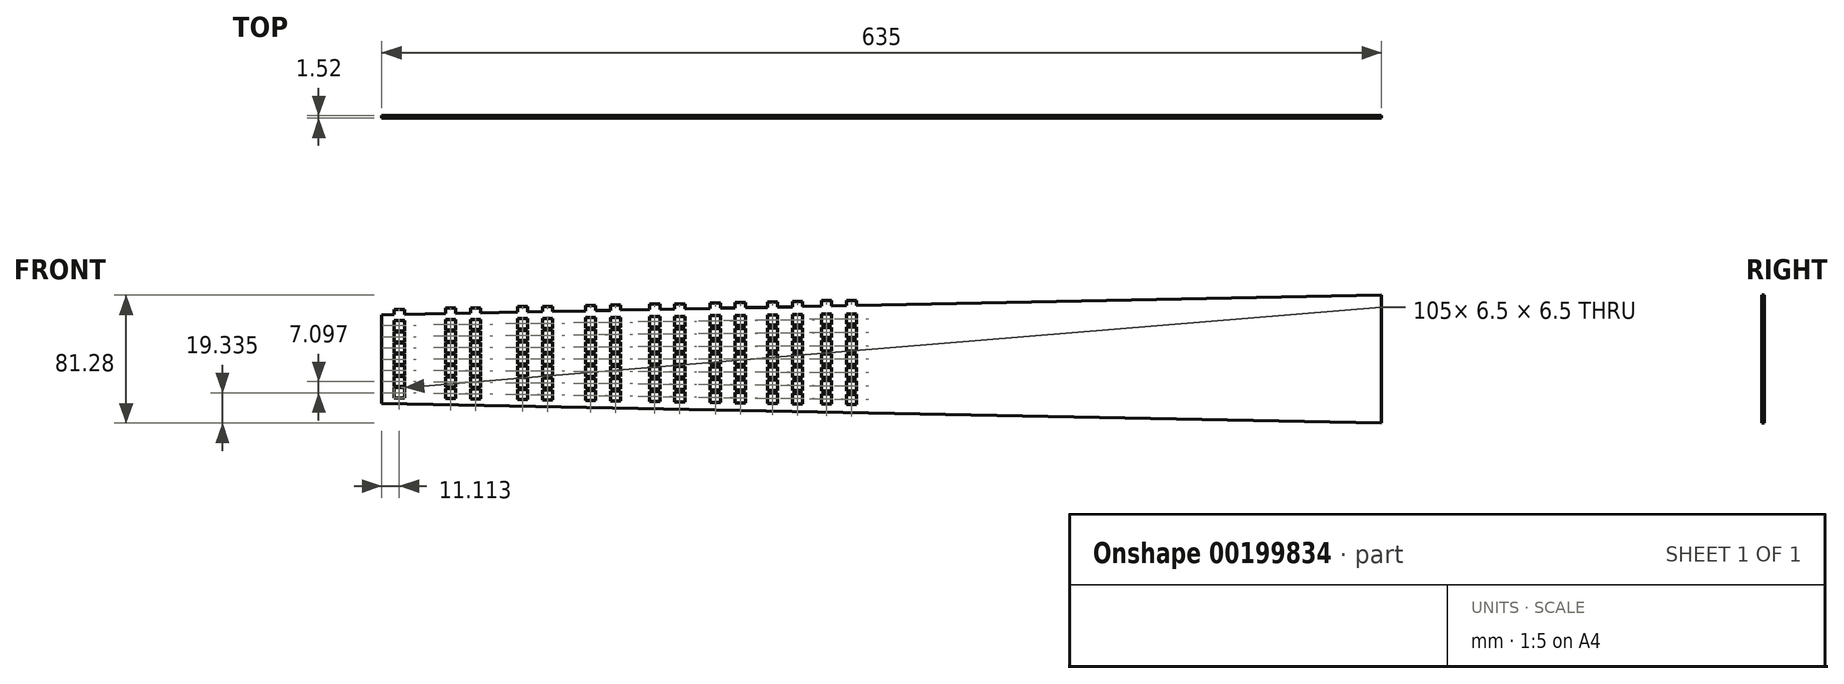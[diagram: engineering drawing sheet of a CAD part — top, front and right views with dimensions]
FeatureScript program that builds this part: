
annotation { "Feature Type Name" : "Feature", "Feature Type Description" : "" }
export const myFeature = defineFeature(function(context is Context, id is Id, definition is map)
    precondition{}
    {
        {
            var Q0;
            Q0=qCreatedBy(makeId("Front.planeOp"),FACE);
            var sketch = newSketch(context, id + "F0", { "sketchPlane" : qUnion([Q0])});
            skLineSegment(sketch, "E0", {"start": v(0, 0) * mm, "end": v(0, 56.39) * mm});
            skLineSegment(sketch, "E1", {"start": v(0, 56.39) * mm, "end": v(304.8, 62.36) * mm});
            skLineSegment(sketch, "E2", {"start": v(635, 68.83) * mm, "end": v(635, -12.45) * mm});
            skLineSegment(sketch, "E3", {"start": v(635, -12.45) * mm, "end": v(304.8, -5.97) * mm});
            skLineSegment(sketch, "E4", {"start": v(0, 28.2) * mm, "end": v(897.35, 28.2) * mm, "construction": true});
            skLineSegment(sketch, "E5", {"start": v(0, 7.05) * mm, "end": v(635, -2.29) * mm, "construction": true});
            skLineSegment(sketch, "E6", {"start": v(0, 21.15) * mm, "end": v(635, 18.03) * mm, "construction": true});
            skLineSegment(sketch, "E7", {"start": v(0, 35.24) * mm, "end": v(635, 38.35) * mm, "construction": true});
            skLineSegment(sketch, "E8", {"start": v(0, 49.34) * mm, "end": v(635, 58.67) * mm, "construction": true});
            skLineSegment(sketch, "E9", {"start": v(11.11, -8.07) * mm, "end": v(11.11, 65.52) * mm, "construction": true});
            skLineSegment(sketch, "E10", {"start": v(59.58, -8.48) * mm, "end": v(59.58, 66.34) * mm, "construction": true});
            skLineSegment(sketch, "E11", {"start": v(43.7, -5.78) * mm, "end": v(43.7, 64.91) * mm, "construction": true});
            skPoint(sketch, "E12", {"position": v(11.11, 6.89) * mm});
            skLineSegment(sketch, "E13.bottom", {"start": v(7.86, 10.14) * mm, "end": v(14.36, 10.14) * mm});
            skLineSegment(sketch, "E13.top", {"start": v(7.86, 3.64) * mm, "end": v(14.36, 3.64) * mm});
            skLineSegment(sketch, "E13.left", {"start": v(7.86, 10.14) * mm, "end": v(7.86, 3.64) * mm});
            skLineSegment(sketch, "E13.right", {"start": v(14.36, 10.14) * mm, "end": v(14.36, 3.64) * mm});
            skLineSegment(sketch, "E14.direction2", {"start": v(7.86, 10.14) * mm, "end": v(7.86, 17.25) * mm, "construction": true});
            skLineSegment(sketch, "E15.bottom", {"start": v(40.46, 9.66) * mm, "end": v(46.96, 9.66) * mm});
            skLineSegment(sketch, "E15.top", {"start": v(40.46, 3.16) * mm, "end": v(46.96, 3.16) * mm});
            skLineSegment(sketch, "E15.left", {"start": v(40.46, 9.66) * mm, "end": v(40.46, 3.16) * mm});
            skLineSegment(sketch, "E15.right", {"start": v(46.96, 9.66) * mm, "end": v(46.96, 3.16) * mm});
            skPoint(sketch, "E15.middle", {"position": v(43.7, 6.4) * mm});
            skLineSegment(sketch, "E16.bottom", {"start": v(62.83, 9.42) * mm, "end": v(56.33, 9.42) * mm});
            skLineSegment(sketch, "E16.top", {"start": v(62.83, 2.92) * mm, "end": v(56.33, 2.92) * mm});
            skLineSegment(sketch, "E16.left", {"start": v(62.83, 9.42) * mm, "end": v(62.83, 2.92) * mm});
            skLineSegment(sketch, "E16.right", {"start": v(56.33, 9.42) * mm, "end": v(56.33, 2.92) * mm});
            skPoint(sketch, "E16.middle", {"position": v(59.58, 6.17) * mm});
            skPoint(sketch, "E17", {"position": v(43.7, 20.93) * mm});
            skPoint(sketch, "E18", {"position": v(59.58, 20.85) * mm});
            skLineSegment(sketch, "E19", {"start": v(89.46, -9.6) * mm, "end": v(89.46, 71.58) * mm, "construction": true});
            skLineSegment(sketch, "E20", {"start": v(105.33, -10.34) * mm, "end": v(105.33, 69.93) * mm, "construction": true});
            skLineSegment(sketch, "E21", {"start": v(132.64, -17.59) * mm, "end": v(132.64, 74.26) * mm, "construction": true});
            skLineSegment(sketch, "E22", {"start": v(148.51, -17.59) * mm, "end": v(148.51, 69.02) * mm, "construction": true});
            skLineSegment(sketch, "E23", {"start": v(173.4, -18.82) * mm, "end": v(173.4, 73.33) * mm, "construction": true});
            skLineSegment(sketch, "E24", {"start": v(189.27, -16.66) * mm, "end": v(189.27, 66.86) * mm, "construction": true});
            skLineSegment(sketch, "E25", {"start": v(451.27, -15.83) * mm, "end": v(451.27, 70.28) * mm, "construction": true});
            skLineSegment(sketch, "E26", {"start": v(227.74, -18.15) * mm, "end": v(227.74, 69.99) * mm, "construction": true});
            skLineSegment(sketch, "E27", {"start": v(264.05, -13.9) * mm, "end": v(264.05, 74.15) * mm, "construction": true});
            skLineSegment(sketch, "E28", {"start": v(298.33, -16.5) * mm, "end": v(298.33, 71.54) * mm, "construction": true});
            skLineSegment(sketch, "E29", {"start": v(330.68, -19.56) * mm, "end": v(330.68, 75.46) * mm, "construction": true});
            skLineSegment(sketch, "E30", {"start": v(361.21, -17.9) * mm, "end": v(361.21, 72.97) * mm, "construction": true});
            skLineSegment(sketch, "E31", {"start": v(390.03, -19.02) * mm, "end": v(390.03, 73.96) * mm, "construction": true});
            skLineSegment(sketch, "E32", {"start": v(417.24, -23.13) * mm, "end": v(417.24, 74.37) * mm, "construction": true});
            skLineSegment(sketch, "E33", {"start": v(442.91, -24.9) * mm, "end": v(442.91, 73.26) * mm, "construction": true});
            skLineSegment(sketch, "E34", {"start": v(467.15, -27.86) * mm, "end": v(467.15, 72.83) * mm, "construction": true});
            skLineSegment(sketch, "E35", {"start": v(492.88, -29.16) * mm, "end": v(492.88, 78.06) * mm, "construction": true});
            skLineSegment(sketch, "E36", {"start": v(513.87, -22.04) * mm, "end": v(513.87, 76.59) * mm, "construction": true});
            skLineSegment(sketch, "E37", {"start": v(533.67, -25.93) * mm, "end": v(533.67, 79.32) * mm, "construction": true});
            skLineSegment(sketch, "E38", {"start": v(602.4, -21.27) * mm, "end": v(602.4, 83.2) * mm, "construction": true});
            skLineSegment(sketch, "E39", {"start": v(570.01, -19.88) * mm, "end": v(570.01, 78.37) * mm, "construction": true});
            skLineSegment(sketch, "E40", {"start": v(586.67, -17.8) * mm, "end": v(586.67, 83.9) * mm, "construction": true});
            skLineSegment(sketch, "E41", {"start": v(552.37, -18.5) * mm, "end": v(552.37, 94.16) * mm, "construction": true});
            skPoint(sketch, "E42", {"position": v(89.46, 5.73) * mm});
            skPoint(sketch, "E43", {"position": v(89.46, 20.7) * mm});
            skPoint(sketch, "E44", {"position": v(105.33, 20.63) * mm});
            skPoint(sketch, "E45", {"position": v(105.33, 5.5) * mm});
            skPoint(sketch, "E46", {"position": v(132.64, 20.5) * mm});
            skPoint(sketch, "E47", {"position": v(132.64, 5.1) * mm});
            skPoint(sketch, "E48", {"position": v(148.51, 20.42) * mm});
            skPoint(sketch, "E49", {"position": v(148.51, 4.87) * mm});
            skPoint(sketch, "E50", {"position": v(173.4, 20.3) * mm});
            skPoint(sketch, "E51", {"position": v(173.4, 4.5) * mm});
            skPoint(sketch, "E52", {"position": v(189.27, 20.22) * mm});
            skPoint(sketch, "E53", {"position": v(227.74, 20.03) * mm});
            skPoint(sketch, "E54", {"position": v(227.74, 3.7) * mm});
            skLineSegment(sketch, "E55", {"start": v(304.8, -5.97) * mm, "end": v(304.8, 62.36) * mm});
            skLineSegment(sketch, "E56", {"start": v(211.87, -18.15) * mm, "end": v(211.87, 88.54) * mm, "construction": true});
            skLineSegment(sketch, "E57", {"start": v(248.18, -17.72) * mm, "end": v(248.18, 84.91) * mm, "construction": true});
            skLineSegment(sketch, "E58", {"start": v(282.45, -20.3) * mm, "end": v(282.45, 79.21) * mm, "construction": true});
            skPoint(sketch, "E59", {"position": v(298.33, 2.66) * mm});
            skPoint(sketch, "E60", {"position": v(298.33, 19.68) * mm});
            skPoint(sketch, "E61", {"position": v(282.45, 19.76) * mm});
            skPoint(sketch, "E62", {"position": v(282.45, 2.9) * mm});
            skPoint(sketch, "E63", {"position": v(264.05, 3.17) * mm});
            skPoint(sketch, "E64", {"position": v(264.05, 19.85) * mm});
            skPoint(sketch, "E65", {"position": v(248.18, 19.93) * mm});
            skPoint(sketch, "E66", {"position": v(248.18, 3.4) * mm});
            skPoint(sketch, "E67", {"position": v(211.87, 20.1) * mm});
            skPoint(sketch, "E68", {"position": v(211.87, 3.93) * mm});
            skLineSegment(sketch, "E69.bottom", {"start": v(86.2, 8.98) * mm, "end": v(92.7, 8.98) * mm});
            skLineSegment(sketch, "E69.top", {"start": v(86.2, 2.48) * mm, "end": v(92.7, 2.48) * mm});
            skLineSegment(sketch, "E69.left", {"start": v(86.2, 8.98) * mm, "end": v(86.2, 2.48) * mm});
            skLineSegment(sketch, "E69.right", {"start": v(92.7, 8.98) * mm, "end": v(92.7, 2.48) * mm});
            skLineSegment(sketch, "E70.bottom", {"start": v(102.08, 8.75) * mm, "end": v(108.58, 8.75) * mm});
            skLineSegment(sketch, "E70.top", {"start": v(102.08, 2.25) * mm, "end": v(108.58, 2.25) * mm});
            skLineSegment(sketch, "E70.left", {"start": v(102.08, 8.75) * mm, "end": v(102.08, 2.25) * mm});
            skLineSegment(sketch, "E70.right", {"start": v(108.58, 8.75) * mm, "end": v(108.58, 2.25) * mm});
            skLineSegment(sketch, "E71.bottom", {"start": v(129.39, 8.35) * mm, "end": v(135.89, 8.35) * mm});
            skLineSegment(sketch, "E71.top", {"start": v(129.39, 1.85) * mm, "end": v(135.89, 1.85) * mm});
            skLineSegment(sketch, "E71.left", {"start": v(129.39, 8.35) * mm, "end": v(129.39, 1.85) * mm});
            skLineSegment(sketch, "E71.right", {"start": v(135.89, 8.35) * mm, "end": v(135.89, 1.85) * mm});
            skLineSegment(sketch, "E72.bottom", {"start": v(145.26, 8.12) * mm, "end": v(151.76, 8.12) * mm});
            skLineSegment(sketch, "E72.top", {"start": v(145.26, 1.62) * mm, "end": v(151.76, 1.62) * mm});
            skLineSegment(sketch, "E72.left", {"start": v(145.26, 8.12) * mm, "end": v(145.26, 1.62) * mm});
            skLineSegment(sketch, "E72.right", {"start": v(151.76, 8.12) * mm, "end": v(151.76, 1.62) * mm});
            skLineSegment(sketch, "E73.bottom", {"start": v(208.62, 7.18) * mm, "end": v(215.12, 7.18) * mm});
            skLineSegment(sketch, "E73.top", {"start": v(208.62, 0.68) * mm, "end": v(215.12, 0.68) * mm});
            skLineSegment(sketch, "E73.left", {"start": v(208.62, 7.18) * mm, "end": v(208.62, 0.68) * mm});
            skLineSegment(sketch, "E73.right", {"start": v(215.12, 7.18) * mm, "end": v(215.12, 0.68) * mm});
            skLineSegment(sketch, "E74.bottom", {"start": v(224.5, 6.95) * mm, "end": v(231, 6.95) * mm});
            skLineSegment(sketch, "E74.top", {"start": v(224.5, 0.45) * mm, "end": v(231, 0.45) * mm});
            skLineSegment(sketch, "E74.left", {"start": v(224.5, 6.95) * mm, "end": v(224.5, 0.45) * mm});
            skLineSegment(sketch, "E74.right", {"start": v(231, 6.95) * mm, "end": v(231, 0.45) * mm});
            skLineSegment(sketch, "E75.bottom", {"start": v(244.93, 6.65) * mm, "end": v(251.43, 6.65) * mm});
            skLineSegment(sketch, "E75.top", {"start": v(244.93, 0.15) * mm, "end": v(251.43, 0.15) * mm});
            skLineSegment(sketch, "E75.left", {"start": v(244.93, 6.65) * mm, "end": v(244.93, 0.15) * mm});
            skLineSegment(sketch, "E75.right", {"start": v(251.43, 6.65) * mm, "end": v(251.43, 0.15) * mm});
            skLineSegment(sketch, "E76.bottom", {"start": v(260.8, 6.42) * mm, "end": v(267.3, 6.42) * mm});
            skLineSegment(sketch, "E76.top", {"start": v(260.8, -0.08) * mm, "end": v(267.3, -0.08) * mm});
            skLineSegment(sketch, "E76.left", {"start": v(260.8, 6.42) * mm, "end": v(260.8, -0.08) * mm});
            skLineSegment(sketch, "E76.right", {"start": v(267.3, 6.42) * mm, "end": v(267.3, -0.08) * mm});
            skLineSegment(sketch, "E77.bottom", {"start": v(279.2, 6.15) * mm, "end": v(285.7, 6.15) * mm});
            skLineSegment(sketch, "E77.top", {"start": v(279.2, -0.35) * mm, "end": v(285.7, -0.35) * mm});
            skLineSegment(sketch, "E77.left", {"start": v(279.2, 6.15) * mm, "end": v(279.2, -0.35) * mm});
            skLineSegment(sketch, "E77.right", {"start": v(285.7, 6.15) * mm, "end": v(285.7, -0.35) * mm});
            skLineSegment(sketch, "E78.bottom", {"start": v(295.08, 5.91) * mm, "end": v(301.58, 5.91) * mm});
            skLineSegment(sketch, "E78.top", {"start": v(295.08, -0.59) * mm, "end": v(301.58, -0.59) * mm});
            skLineSegment(sketch, "E78.left", {"start": v(295.08, 5.91) * mm, "end": v(295.08, -0.59) * mm});
            skLineSegment(sketch, "E78.right", {"start": v(301.58, 5.91) * mm, "end": v(301.58, -0.59) * mm});
            skLineSegment(sketch, "E79.bottom", {"start": v(170.14, 7.75) * mm, "end": v(176.64, 7.75) * mm});
            skLineSegment(sketch, "E79.top", {"start": v(170.14, 1.25) * mm, "end": v(176.64, 1.25) * mm});
            skLineSegment(sketch, "E79.left", {"start": v(170.14, 7.75) * mm, "end": v(170.14, 1.25) * mm});
            skLineSegment(sketch, "E79.right", {"start": v(176.64, 7.75) * mm, "end": v(176.64, 1.25) * mm});
            skPoint(sketch, "E80", {"position": v(304.8, 62.36) * mm});
            skPoint(sketch, "E81", {"position": v(304.8, -5.97) * mm});
            skPoint(sketch, "E82.orphan", {"position": v(304.8, 80.2) * mm});
            skLineSegment(sketch, "E83", {"start": v(304.8, 62.36) * mm, "end": v(635, 68.83) * mm});
            skLineSegment(sketch, "E84", {"start": v(304.8, -5.97) * mm, "end": v(0, 0) * mm});
            skLineSegment(sketch, "E85.0.1.0", {"start": v(40.46, 16.94) * mm, "end": v(46.96, 16.94) * mm});
            skLineSegment(sketch, "E85.0.1.1", {"start": v(40.46, 16.94) * mm, "end": v(40.46, 10.44) * mm});
            skLineSegment(sketch, "E85.0.1.2", {"start": v(46.96, 16.94) * mm, "end": v(46.96, 10.44) * mm});
            skLineSegment(sketch, "E85.0.1.3", {"start": v(40.46, 10.44) * mm, "end": v(46.96, 10.44) * mm});
            skLineSegment(sketch, "E85.0.2.0", {"start": v(40.46, 24.23) * mm, "end": v(46.96, 24.23) * mm});
            skLineSegment(sketch, "E85.0.2.1", {"start": v(40.46, 24.23) * mm, "end": v(40.46, 17.73) * mm});
            skLineSegment(sketch, "E85.0.2.2", {"start": v(46.96, 24.23) * mm, "end": v(46.96, 17.73) * mm});
            skLineSegment(sketch, "E85.0.2.3", {"start": v(40.46, 17.73) * mm, "end": v(46.96, 17.73) * mm});
            skLineSegment(sketch, "E85.0.3.0", {"start": v(40.46, 31.52) * mm, "end": v(46.96, 31.52) * mm});
            skLineSegment(sketch, "E85.0.3.1", {"start": v(40.46, 31.52) * mm, "end": v(40.46, 25.02) * mm});
            skLineSegment(sketch, "E85.0.3.2", {"start": v(46.96, 31.52) * mm, "end": v(46.96, 25.02) * mm});
            skLineSegment(sketch, "E85.0.3.3", {"start": v(40.46, 25.02) * mm, "end": v(46.96, 25.02) * mm});
            skLineSegment(sketch, "E85.direction1", {"start": v(40.46, 9.66) * mm, "end": v(65.86, 9.66) * mm, "construction": true});
            skLineSegment(sketch, "E85.direction2", {"start": v(40.46, 9.66) * mm, "end": v(40.46, 16.94) * mm, "construction": true});
            skLineSegment(sketch, "E86.0.1.0", {"start": v(56.33, 16.77) * mm, "end": v(56.33, 10.27) * mm});
            skLineSegment(sketch, "E86.0.1.1", {"start": v(62.83, 10.27) * mm, "end": v(56.33, 10.27) * mm});
            skLineSegment(sketch, "E86.0.1.2", {"start": v(62.83, 16.77) * mm, "end": v(56.33, 16.77) * mm});
            skLineSegment(sketch, "E86.0.1.3", {"start": v(62.83, 16.77) * mm, "end": v(62.83, 10.27) * mm});
            skPoint(sketch, "E86.0.1.4", {"position": v(59.58, 13.52) * mm});
            skLineSegment(sketch, "E86.0.2.0", {"start": v(56.33, 24.12) * mm, "end": v(56.33, 17.62) * mm});
            skLineSegment(sketch, "E86.0.2.1", {"start": v(62.83, 17.62) * mm, "end": v(56.33, 17.62) * mm});
            skLineSegment(sketch, "E86.0.2.2", {"start": v(62.83, 24.12) * mm, "end": v(56.33, 24.12) * mm});
            skLineSegment(sketch, "E86.0.2.3", {"start": v(62.83, 24.12) * mm, "end": v(62.83, 17.62) * mm});
            skPoint(sketch, "E86.0.2.4", {"position": v(59.58, 20.87) * mm});
            skLineSegment(sketch, "E86.0.3.0", {"start": v(56.33, 31.47) * mm, "end": v(56.33, 24.97) * mm});
            skLineSegment(sketch, "E86.0.3.1", {"start": v(62.83, 24.97) * mm, "end": v(56.33, 24.97) * mm});
            skLineSegment(sketch, "E86.0.3.2", {"start": v(62.83, 31.47) * mm, "end": v(56.33, 31.47) * mm});
            skLineSegment(sketch, "E86.0.3.3", {"start": v(62.83, 31.47) * mm, "end": v(62.83, 24.97) * mm});
            skPoint(sketch, "E86.0.3.4", {"position": v(59.58, 28.22) * mm});
            skLineSegment(sketch, "E86.direction1", {"start": v(56.33, 2.92) * mm, "end": v(83.32, 2.92) * mm, "construction": true});
            skLineSegment(sketch, "E86.direction2", {"start": v(56.33, 2.92) * mm, "end": v(56.33, 10.27) * mm, "construction": true});
            skLineSegment(sketch, "E87.0.1.0", {"start": v(86.2, 10) * mm, "end": v(92.7, 10) * mm});
            skLineSegment(sketch, "E87.0.1.1", {"start": v(92.7, 16.5) * mm, "end": v(92.7, 10) * mm});
            skPoint(sketch, "E87.0.1.2", {"position": v(89.46, 13.24) * mm});
            skLineSegment(sketch, "E87.0.1.3", {"start": v(86.2, 16.5) * mm, "end": v(86.2, 10) * mm});
            skLineSegment(sketch, "E87.0.1.4", {"start": v(86.2, 16.5) * mm, "end": v(92.7, 16.5) * mm});
            skPoint(sketch, "E87.0.1.5", {"position": v(89.46, 13.24) * mm});
            skLineSegment(sketch, "E87.0.2.0", {"start": v(86.2, 17.5) * mm, "end": v(92.7, 17.5) * mm});
            skLineSegment(sketch, "E87.0.2.1", {"start": v(92.7, 24) * mm, "end": v(92.7, 17.5) * mm});
            skPoint(sketch, "E87.0.2.2", {"position": v(89.46, 20.76) * mm});
            skLineSegment(sketch, "E87.0.2.3", {"start": v(86.2, 24) * mm, "end": v(86.2, 17.5) * mm});
            skLineSegment(sketch, "E87.0.2.4", {"start": v(86.2, 24) * mm, "end": v(92.7, 24) * mm});
            skPoint(sketch, "E87.0.2.5", {"position": v(89.46, 20.76) * mm});
            skLineSegment(sketch, "E87.0.3.0", {"start": v(86.2, 25.02) * mm, "end": v(92.7, 25.02) * mm});
            skLineSegment(sketch, "E87.0.3.1", {"start": v(92.7, 31.52) * mm, "end": v(92.7, 25.02) * mm});
            skPoint(sketch, "E87.0.3.2", {"position": v(89.46, 28.27) * mm});
            skLineSegment(sketch, "E87.0.3.3", {"start": v(86.2, 31.52) * mm, "end": v(86.2, 25.02) * mm});
            skLineSegment(sketch, "E87.0.3.4", {"start": v(86.2, 31.52) * mm, "end": v(92.7, 31.52) * mm});
            skPoint(sketch, "E87.0.3.5", {"position": v(89.46, 28.27) * mm});
            skLineSegment(sketch, "E87.direction1", {"start": v(86.2, 2.48) * mm, "end": v(111.6, 2.48) * mm, "construction": true});
            skLineSegment(sketch, "E87.direction2", {"start": v(86.2, 2.48) * mm, "end": v(86.2, 10) * mm, "construction": true});
            skLineSegment(sketch, "E88.0.1.0", {"start": v(102.08, 9.82) * mm, "end": v(108.58, 9.82) * mm});
            skLineSegment(sketch, "E88.0.1.1", {"start": v(102.08, 16.32) * mm, "end": v(102.08, 9.82) * mm});
            skLineSegment(sketch, "E88.0.1.2", {"start": v(102.08, 16.32) * mm, "end": v(108.58, 16.32) * mm});
            skLineSegment(sketch, "E88.0.1.3", {"start": v(108.58, 16.32) * mm, "end": v(108.58, 9.82) * mm});
            skPoint(sketch, "E88.0.1.4", {"position": v(105.33, 13.07) * mm});
            skPoint(sketch, "E88.0.1.5", {"position": v(105.33, 13.07) * mm});
            skLineSegment(sketch, "E88.0.2.0", {"start": v(102.08, 17.4) * mm, "end": v(108.58, 17.4) * mm});
            skLineSegment(sketch, "E88.0.2.1", {"start": v(102.08, 23.9) * mm, "end": v(102.08, 17.4) * mm});
            skLineSegment(sketch, "E88.0.2.2", {"start": v(102.08, 23.9) * mm, "end": v(108.58, 23.9) * mm});
            skLineSegment(sketch, "E88.0.2.3", {"start": v(108.58, 23.9) * mm, "end": v(108.58, 17.4) * mm});
            skPoint(sketch, "E88.0.2.4", {"position": v(105.33, 20.64) * mm});
            skPoint(sketch, "E88.0.2.5", {"position": v(105.33, 20.64) * mm});
            skLineSegment(sketch, "E88.0.3.0", {"start": v(102.08, 24.97) * mm, "end": v(108.58, 24.97) * mm});
            skLineSegment(sketch, "E88.0.3.1", {"start": v(102.08, 31.47) * mm, "end": v(102.08, 24.97) * mm});
            skLineSegment(sketch, "E88.0.3.2", {"start": v(102.08, 31.47) * mm, "end": v(108.58, 31.47) * mm});
            skLineSegment(sketch, "E88.0.3.3", {"start": v(108.58, 31.47) * mm, "end": v(108.58, 24.97) * mm});
            skPoint(sketch, "E88.0.3.4", {"position": v(105.33, 28.22) * mm});
            skPoint(sketch, "E88.0.3.5", {"position": v(105.33, 28.22) * mm});
            skLineSegment(sketch, "E88.direction1", {"start": v(102.08, 2.25) * mm, "end": v(127.48, 2.25) * mm, "construction": true});
            skLineSegment(sketch, "E88.direction2", {"start": v(102.08, 2.25) * mm, "end": v(102.08, 9.82) * mm, "construction": true});
            skLineSegment(sketch, "E89.0.0.4", {"start": v(86.2, 32.53) * mm, "end": v(92.7, 32.53) * mm});
            skLineSegment(sketch, "E89.3.0.4", {"start": v(92.7, 39.03) * mm, "end": v(92.7, 32.53) * mm});
            skPoint(sketch, "E89.6.0.4", {"position": v(89.46, 35.78) * mm});
            skLineSegment(sketch, "E89.7.0.4", {"start": v(86.2, 39.03) * mm, "end": v(86.2, 32.53) * mm});
            skLineSegment(sketch, "E89.10.0.4", {"start": v(86.2, 39.03) * mm, "end": v(92.7, 39.03) * mm});
            skPoint(sketch, "E89.13.0.4", {"position": v(89.46, 35.78) * mm});
            skLineSegment(sketch, "E89.0.0.5", {"start": v(86.2, 40.04) * mm, "end": v(92.7, 40.04) * mm});
            skLineSegment(sketch, "E89.3.0.5", {"start": v(92.7, 46.54) * mm, "end": v(92.7, 40.04) * mm});
            skPoint(sketch, "E89.6.0.5", {"position": v(89.46, 43.29) * mm});
            skLineSegment(sketch, "E89.7.0.5", {"start": v(86.2, 46.54) * mm, "end": v(86.2, 40.04) * mm});
            skLineSegment(sketch, "E89.10.0.5", {"start": v(86.2, 46.54) * mm, "end": v(92.7, 46.54) * mm});
            skPoint(sketch, "E89.13.0.5", {"position": v(89.46, 43.29) * mm});
            skLineSegment(sketch, "E89.0.0.6", {"start": v(86.2, 47.55) * mm, "end": v(92.7, 47.55) * mm});
            skLineSegment(sketch, "E89.3.0.6", {"start": v(92.7, 54.05) * mm, "end": v(92.7, 47.55) * mm});
            skPoint(sketch, "E89.6.0.6", {"position": v(89.46, 50.8) * mm});
            skLineSegment(sketch, "E89.7.0.6", {"start": v(86.2, 54.05) * mm, "end": v(86.2, 47.55) * mm});
            skLineSegment(sketch, "E89.10.0.6", {"start": v(86.2, 54.05) * mm, "end": v(92.7, 54.05) * mm});
            skPoint(sketch, "E89.13.0.6", {"position": v(89.46, 50.8) * mm});
            skLineSegment(sketch, "E89.0.0.7", {"start": v(86.2, 55.06) * mm, "end": v(92.7, 55.06) * mm});
            skLineSegment(sketch, "E89.3.0.7", {"start": v(92.7, 61.56) * mm, "end": v(92.7, 55.06) * mm});
            skPoint(sketch, "E89.6.0.7", {"position": v(89.46, 58.3) * mm});
            skLineSegment(sketch, "E89.7.0.7", {"start": v(86.2, 61.56) * mm, "end": v(86.2, 55.06) * mm});
            skLineSegment(sketch, "E89.10.0.7", {"start": v(86.2, 61.56) * mm, "end": v(92.7, 61.56) * mm});
            skPoint(sketch, "E89.13.0.7", {"position": v(89.46, 58.3) * mm});
            skLineSegment(sketch, "E90.0.0.4", {"start": v(40.46, 38.8) * mm, "end": v(46.96, 38.8) * mm});
            skLineSegment(sketch, "E90.3.0.4", {"start": v(40.46, 38.8) * mm, "end": v(40.46, 32.3) * mm});
            skLineSegment(sketch, "E90.6.0.4", {"start": v(46.96, 38.8) * mm, "end": v(46.96, 32.3) * mm});
            skLineSegment(sketch, "E90.9.0.4", {"start": v(40.46, 32.3) * mm, "end": v(46.96, 32.3) * mm});
            skLineSegment(sketch, "E90.0.0.5", {"start": v(40.46, 46.1) * mm, "end": v(46.96, 46.1) * mm});
            skLineSegment(sketch, "E90.3.0.5", {"start": v(40.46, 46.1) * mm, "end": v(40.46, 39.6) * mm});
            skLineSegment(sketch, "E90.6.0.5", {"start": v(46.96, 46.1) * mm, "end": v(46.96, 39.6) * mm});
            skLineSegment(sketch, "E90.9.0.5", {"start": v(40.46, 39.6) * mm, "end": v(46.96, 39.6) * mm});
            skLineSegment(sketch, "E90.0.0.6", {"start": v(40.46, 53.38) * mm, "end": v(46.96, 53.38) * mm});
            skLineSegment(sketch, "E90.3.0.6", {"start": v(40.46, 53.38) * mm, "end": v(40.46, 46.88) * mm});
            skLineSegment(sketch, "E90.6.0.6", {"start": v(46.96, 53.38) * mm, "end": v(46.96, 46.88) * mm});
            skLineSegment(sketch, "E90.9.0.6", {"start": v(40.46, 46.88) * mm, "end": v(46.96, 46.88) * mm});
            skLineSegment(sketch, "E90.0.0.7", {"start": v(40.46, 60.67) * mm, "end": v(46.96, 60.67) * mm});
            skLineSegment(sketch, "E90.3.0.7", {"start": v(40.46, 60.67) * mm, "end": v(40.46, 54.17) * mm});
            skLineSegment(sketch, "E90.6.0.7", {"start": v(46.96, 60.67) * mm, "end": v(46.96, 54.17) * mm});
            skLineSegment(sketch, "E90.9.0.7", {"start": v(40.46, 54.17) * mm, "end": v(46.96, 54.17) * mm});
            skLineSegment(sketch, "E91.0.0.4", {"start": v(56.33, 38.82) * mm, "end": v(56.33, 32.32) * mm});
            skLineSegment(sketch, "E91.3.0.4", {"start": v(62.83, 32.32) * mm, "end": v(56.33, 32.32) * mm});
            skLineSegment(sketch, "E91.6.0.4", {"start": v(62.83, 38.82) * mm, "end": v(56.33, 38.82) * mm});
            skLineSegment(sketch, "E91.9.0.4", {"start": v(62.83, 38.82) * mm, "end": v(62.83, 32.32) * mm});
            skPoint(sketch, "E91.12.0.4", {"position": v(59.58, 35.57) * mm});
            skLineSegment(sketch, "E91.0.0.5", {"start": v(56.33, 46.16) * mm, "end": v(56.33, 39.66) * mm});
            skLineSegment(sketch, "E91.3.0.5", {"start": v(62.83, 39.66) * mm, "end": v(56.33, 39.66) * mm});
            skLineSegment(sketch, "E91.6.0.5", {"start": v(62.83, 46.16) * mm, "end": v(56.33, 46.16) * mm});
            skLineSegment(sketch, "E91.9.0.5", {"start": v(62.83, 46.16) * mm, "end": v(62.83, 39.66) * mm});
            skPoint(sketch, "E91.12.0.5", {"position": v(59.58, 42.91) * mm});
            skLineSegment(sketch, "E91.0.0.6", {"start": v(56.33, 53.51) * mm, "end": v(56.33, 47.01) * mm});
            skLineSegment(sketch, "E91.3.0.6", {"start": v(62.83, 47.01) * mm, "end": v(56.33, 47.01) * mm});
            skLineSegment(sketch, "E91.6.0.6", {"start": v(62.83, 53.51) * mm, "end": v(56.33, 53.51) * mm});
            skLineSegment(sketch, "E91.9.0.6", {"start": v(62.83, 53.51) * mm, "end": v(62.83, 47.01) * mm});
            skPoint(sketch, "E91.12.0.6", {"position": v(59.58, 50.26) * mm});
            skLineSegment(sketch, "E91.0.0.7", {"start": v(56.33, 60.86) * mm, "end": v(56.33, 54.36) * mm});
            skLineSegment(sketch, "E91.3.0.7", {"start": v(62.83, 54.36) * mm, "end": v(56.33, 54.36) * mm});
            skLineSegment(sketch, "E91.6.0.7", {"start": v(62.83, 60.86) * mm, "end": v(56.33, 60.86) * mm});
            skLineSegment(sketch, "E91.9.0.7", {"start": v(62.83, 60.86) * mm, "end": v(62.83, 54.36) * mm});
            skPoint(sketch, "E91.12.0.7", {"position": v(59.58, 57.61) * mm});
            skLineSegment(sketch, "E92.0.0.4", {"start": v(102.08, 32.54) * mm, "end": v(108.58, 32.54) * mm});
            skLineSegment(sketch, "E92.3.0.4", {"start": v(102.08, 39.04) * mm, "end": v(102.08, 32.54) * mm});
            skLineSegment(sketch, "E92.6.0.4", {"start": v(102.08, 39.04) * mm, "end": v(108.58, 39.04) * mm});
            skLineSegment(sketch, "E92.9.0.4", {"start": v(108.58, 39.04) * mm, "end": v(108.58, 32.54) * mm});
            skPoint(sketch, "E92.12.0.4", {"position": v(105.33, 35.79) * mm});
            skPoint(sketch, "E92.13.0.4", {"position": v(105.33, 35.79) * mm});
            skLineSegment(sketch, "E92.0.0.5", {"start": v(102.08, 40.1) * mm, "end": v(108.58, 40.1) * mm});
            skLineSegment(sketch, "E92.3.0.5", {"start": v(102.08, 46.6) * mm, "end": v(102.08, 40.1) * mm});
            skLineSegment(sketch, "E92.6.0.5", {"start": v(102.08, 46.6) * mm, "end": v(108.58, 46.6) * mm});
            skLineSegment(sketch, "E92.9.0.5", {"start": v(108.58, 46.6) * mm, "end": v(108.58, 40.1) * mm});
            skPoint(sketch, "E92.12.0.5", {"position": v(105.33, 43.36) * mm});
            skPoint(sketch, "E92.13.0.5", {"position": v(105.33, 43.36) * mm});
            skLineSegment(sketch, "E92.0.0.6", {"start": v(102.08, 47.68) * mm, "end": v(108.58, 47.68) * mm});
            skLineSegment(sketch, "E92.3.0.6", {"start": v(102.08, 54.18) * mm, "end": v(102.08, 47.68) * mm});
            skLineSegment(sketch, "E92.6.0.6", {"start": v(102.08, 54.18) * mm, "end": v(108.58, 54.18) * mm});
            skLineSegment(sketch, "E92.9.0.6", {"start": v(108.58, 54.18) * mm, "end": v(108.58, 47.68) * mm});
            skPoint(sketch, "E92.12.0.6", {"position": v(105.33, 50.93) * mm});
            skPoint(sketch, "E92.13.0.6", {"position": v(105.33, 50.93) * mm});
            skLineSegment(sketch, "E92.0.0.7", {"start": v(102.08, 55.25) * mm, "end": v(108.58, 55.25) * mm});
            skLineSegment(sketch, "E92.3.0.7", {"start": v(102.08, 61.75) * mm, "end": v(102.08, 55.25) * mm});
            skLineSegment(sketch, "E92.6.0.7", {"start": v(102.08, 61.75) * mm, "end": v(108.58, 61.75) * mm});
            skLineSegment(sketch, "E92.9.0.7", {"start": v(108.58, 61.75) * mm, "end": v(108.58, 55.25) * mm});
            skPoint(sketch, "E92.12.0.7", {"position": v(105.33, 58.5) * mm});
            skPoint(sketch, "E92.13.0.7", {"position": v(105.33, 58.5) * mm});
            skLineSegment(sketch, "E93.0.1.0", {"start": v(129.39, 9.57) * mm, "end": v(135.89, 9.57) * mm});
            skPoint(sketch, "E93.0.1.1", {"position": v(132.64, 12.82) * mm});
            skLineSegment(sketch, "E93.0.1.2", {"start": v(129.39, 16.07) * mm, "end": v(135.89, 16.07) * mm});
            skLineSegment(sketch, "E93.0.1.3", {"start": v(135.89, 16.07) * mm, "end": v(135.89, 9.57) * mm});
            skLineSegment(sketch, "E93.0.1.4", {"start": v(129.39, 16.07) * mm, "end": v(129.39, 9.57) * mm});
            skPoint(sketch, "E93.0.1.5", {"position": v(132.64, 12.82) * mm});
            skLineSegment(sketch, "E93.0.2.0", {"start": v(129.39, 17.3) * mm, "end": v(135.89, 17.3) * mm});
            skPoint(sketch, "E93.0.2.1", {"position": v(132.64, 20.54) * mm});
            skLineSegment(sketch, "E93.0.2.2", {"start": v(129.39, 23.8) * mm, "end": v(135.89, 23.8) * mm});
            skLineSegment(sketch, "E93.0.2.3", {"start": v(135.89, 23.8) * mm, "end": v(135.89, 17.3) * mm});
            skLineSegment(sketch, "E93.0.2.4", {"start": v(129.39, 23.8) * mm, "end": v(129.39, 17.3) * mm});
            skPoint(sketch, "E93.0.2.5", {"position": v(132.64, 20.54) * mm});
            skLineSegment(sketch, "E93.0.3.0", {"start": v(129.39, 25.01) * mm, "end": v(135.89, 25.01) * mm});
            skPoint(sketch, "E93.0.3.1", {"position": v(132.64, 28.26) * mm});
            skLineSegment(sketch, "E93.0.3.2", {"start": v(129.39, 31.51) * mm, "end": v(135.89, 31.51) * mm});
            skLineSegment(sketch, "E93.0.3.3", {"start": v(135.89, 31.51) * mm, "end": v(135.89, 25.01) * mm});
            skLineSegment(sketch, "E93.0.3.4", {"start": v(129.39, 31.51) * mm, "end": v(129.39, 25.01) * mm});
            skPoint(sketch, "E93.0.3.5", {"position": v(132.64, 28.26) * mm});
            skLineSegment(sketch, "E93.0.4.0", {"start": v(129.39, 32.74) * mm, "end": v(135.89, 32.74) * mm});
            skPoint(sketch, "E93.0.4.1", {"position": v(132.64, 35.99) * mm});
            skLineSegment(sketch, "E93.0.4.2", {"start": v(129.39, 39.24) * mm, "end": v(135.89, 39.24) * mm});
            skLineSegment(sketch, "E93.0.4.3", {"start": v(135.89, 39.24) * mm, "end": v(135.89, 32.74) * mm});
            skLineSegment(sketch, "E93.0.4.4", {"start": v(129.39, 39.24) * mm, "end": v(129.39, 32.74) * mm});
            skPoint(sketch, "E93.0.4.5", {"position": v(132.64, 35.99) * mm});
            skLineSegment(sketch, "E93.0.5.0", {"start": v(129.39, 40.46) * mm, "end": v(135.89, 40.46) * mm});
            skPoint(sketch, "E93.0.5.1", {"position": v(132.64, 43.7) * mm});
            skLineSegment(sketch, "E93.0.5.2", {"start": v(129.39, 46.96) * mm, "end": v(135.89, 46.96) * mm});
            skLineSegment(sketch, "E93.0.5.3", {"start": v(135.89, 46.96) * mm, "end": v(135.89, 40.46) * mm});
            skLineSegment(sketch, "E93.0.5.4", {"start": v(129.39, 46.96) * mm, "end": v(129.39, 40.46) * mm});
            skPoint(sketch, "E93.0.5.5", {"position": v(132.64, 43.7) * mm});
            skLineSegment(sketch, "E93.0.6.0", {"start": v(129.39, 48.18) * mm, "end": v(135.89, 48.18) * mm});
            skPoint(sketch, "E93.0.6.1", {"position": v(132.64, 51.43) * mm});
            skLineSegment(sketch, "E93.0.6.2", {"start": v(129.39, 54.68) * mm, "end": v(135.89, 54.68) * mm});
            skLineSegment(sketch, "E93.0.6.3", {"start": v(135.89, 54.68) * mm, "end": v(135.89, 48.18) * mm});
            skLineSegment(sketch, "E93.0.6.4", {"start": v(129.39, 54.68) * mm, "end": v(129.39, 48.18) * mm});
            skPoint(sketch, "E93.0.6.5", {"position": v(132.64, 51.43) * mm});
            skLineSegment(sketch, "E93.0.7.0", {"start": v(129.39, 55.9) * mm, "end": v(135.89, 55.9) * mm});
            skPoint(sketch, "E93.0.7.1", {"position": v(132.64, 59.15) * mm});
            skLineSegment(sketch, "E93.0.7.2", {"start": v(129.39, 62.4) * mm, "end": v(135.89, 62.4) * mm});
            skLineSegment(sketch, "E93.0.7.3", {"start": v(135.89, 62.4) * mm, "end": v(135.89, 55.9) * mm});
            skLineSegment(sketch, "E93.0.7.4", {"start": v(129.39, 62.4) * mm, "end": v(129.39, 55.9) * mm});
            skPoint(sketch, "E93.0.7.5", {"position": v(132.64, 59.15) * mm});
            skLineSegment(sketch, "E93.direction1", {"start": v(129.39, 1.85) * mm, "end": v(154.79, 1.85) * mm, "construction": true});
            skLineSegment(sketch, "E93.direction2", {"start": v(129.39, 1.85) * mm, "end": v(129.39, 9.57) * mm, "construction": true});
            skLineSegment(sketch, "E94.0.1.0", {"start": v(145.26, 15.9) * mm, "end": v(145.26, 9.4) * mm});
            skLineSegment(sketch, "E94.0.1.1", {"start": v(145.26, 9.4) * mm, "end": v(151.76, 9.4) * mm});
            skLineSegment(sketch, "E94.0.1.2", {"start": v(151.76, 15.9) * mm, "end": v(151.76, 9.4) * mm});
            skPoint(sketch, "E94.0.1.3", {"position": v(148.51, 12.65) * mm});
            skLineSegment(sketch, "E94.0.1.4", {"start": v(145.26, 15.9) * mm, "end": v(151.76, 15.9) * mm});
            skPoint(sketch, "E94.0.1.5", {"position": v(148.51, 12.65) * mm});
            skLineSegment(sketch, "E94.0.2.0", {"start": v(145.26, 23.69) * mm, "end": v(145.26, 17.19) * mm});
            skLineSegment(sketch, "E94.0.2.1", {"start": v(145.26, 17.19) * mm, "end": v(151.76, 17.19) * mm});
            skLineSegment(sketch, "E94.0.2.2", {"start": v(151.76, 23.69) * mm, "end": v(151.76, 17.19) * mm});
            skPoint(sketch, "E94.0.2.3", {"position": v(148.51, 20.44) * mm});
            skLineSegment(sketch, "E94.0.2.4", {"start": v(145.26, 23.69) * mm, "end": v(151.76, 23.69) * mm});
            skPoint(sketch, "E94.0.2.5", {"position": v(148.51, 20.44) * mm});
            skLineSegment(sketch, "E94.0.3.0", {"start": v(145.26, 31.47) * mm, "end": v(145.26, 24.97) * mm});
            skLineSegment(sketch, "E94.0.3.1", {"start": v(145.26, 24.97) * mm, "end": v(151.76, 24.97) * mm});
            skLineSegment(sketch, "E94.0.3.2", {"start": v(151.76, 31.47) * mm, "end": v(151.76, 24.97) * mm});
            skPoint(sketch, "E94.0.3.3", {"position": v(148.51, 28.22) * mm});
            skLineSegment(sketch, "E94.0.3.4", {"start": v(145.26, 31.47) * mm, "end": v(151.76, 31.47) * mm});
            skPoint(sketch, "E94.0.3.5", {"position": v(148.51, 28.22) * mm});
            skLineSegment(sketch, "E94.0.4.0", {"start": v(145.26, 39.26) * mm, "end": v(145.26, 32.76) * mm});
            skLineSegment(sketch, "E94.0.4.1", {"start": v(145.26, 32.76) * mm, "end": v(151.76, 32.76) * mm});
            skLineSegment(sketch, "E94.0.4.2", {"start": v(151.76, 39.26) * mm, "end": v(151.76, 32.76) * mm});
            skPoint(sketch, "E94.0.4.3", {"position": v(148.51, 36) * mm});
            skLineSegment(sketch, "E94.0.4.4", {"start": v(145.26, 39.26) * mm, "end": v(151.76, 39.26) * mm});
            skPoint(sketch, "E94.0.4.5", {"position": v(148.51, 36) * mm});
            skLineSegment(sketch, "E94.0.5.0", {"start": v(145.26, 47.04) * mm, "end": v(145.26, 40.54) * mm});
            skLineSegment(sketch, "E94.0.5.1", {"start": v(145.26, 40.54) * mm, "end": v(151.76, 40.54) * mm});
            skLineSegment(sketch, "E94.0.5.2", {"start": v(151.76, 47.04) * mm, "end": v(151.76, 40.54) * mm});
            skPoint(sketch, "E94.0.5.3", {"position": v(148.51, 43.8) * mm});
            skLineSegment(sketch, "E94.0.5.4", {"start": v(145.26, 47.04) * mm, "end": v(151.76, 47.04) * mm});
            skPoint(sketch, "E94.0.5.5", {"position": v(148.51, 43.8) * mm});
            skLineSegment(sketch, "E94.0.6.0", {"start": v(145.26, 54.83) * mm, "end": v(145.26, 48.33) * mm});
            skLineSegment(sketch, "E94.0.6.1", {"start": v(145.26, 48.33) * mm, "end": v(151.76, 48.33) * mm});
            skLineSegment(sketch, "E94.0.6.2", {"start": v(151.76, 54.83) * mm, "end": v(151.76, 48.33) * mm});
            skPoint(sketch, "E94.0.6.3", {"position": v(148.51, 51.58) * mm});
            skLineSegment(sketch, "E94.0.6.4", {"start": v(145.26, 54.83) * mm, "end": v(151.76, 54.83) * mm});
            skPoint(sketch, "E94.0.6.5", {"position": v(148.51, 51.58) * mm});
            skLineSegment(sketch, "E94.0.7.0", {"start": v(145.26, 62.61) * mm, "end": v(145.26, 56.11) * mm});
            skLineSegment(sketch, "E94.0.7.1", {"start": v(145.26, 56.11) * mm, "end": v(151.76, 56.11) * mm});
            skLineSegment(sketch, "E94.0.7.2", {"start": v(151.76, 62.61) * mm, "end": v(151.76, 56.11) * mm});
            skPoint(sketch, "E94.0.7.3", {"position": v(148.51, 59.36) * mm});
            skLineSegment(sketch, "E94.0.7.4", {"start": v(145.26, 62.61) * mm, "end": v(151.76, 62.61) * mm});
            skPoint(sketch, "E94.0.7.5", {"position": v(148.51, 59.36) * mm});
            skLineSegment(sketch, "E94.direction1", {"start": v(145.26, 1.62) * mm, "end": v(172.25, 1.62) * mm, "construction": true});
            skLineSegment(sketch, "E94.direction2", {"start": v(145.26, 1.62) * mm, "end": v(145.26, 9.4) * mm, "construction": true});
            skPoint(sketch, "E95.0.1.0", {"position": v(173.4, 12.42) * mm});
            skLineSegment(sketch, "E95.0.1.1", {"start": v(170.14, 9.17) * mm, "end": v(176.64, 9.17) * mm});
            skLineSegment(sketch, "E95.0.1.2", {"start": v(176.64, 15.67) * mm, "end": v(176.64, 9.17) * mm});
            skLineSegment(sketch, "E95.0.1.3", {"start": v(170.14, 15.67) * mm, "end": v(170.14, 9.17) * mm});
            skLineSegment(sketch, "E95.0.1.4", {"start": v(170.14, 15.67) * mm, "end": v(176.64, 15.67) * mm});
            skPoint(sketch, "E95.0.1.5", {"position": v(173.4, 12.42) * mm});
            skPoint(sketch, "E95.0.1.6", {"position": v(173.4, 12.42) * mm});
            skPoint(sketch, "E95.0.2.0", {"position": v(173.4, 20.34) * mm});
            skLineSegment(sketch, "E95.0.2.1", {"start": v(170.14, 17.1) * mm, "end": v(176.64, 17.1) * mm});
            skLineSegment(sketch, "E95.0.2.2", {"start": v(176.64, 23.6) * mm, "end": v(176.64, 17.1) * mm});
            skLineSegment(sketch, "E95.0.2.3", {"start": v(170.14, 23.6) * mm, "end": v(170.14, 17.1) * mm});
            skLineSegment(sketch, "E95.0.2.4", {"start": v(170.14, 23.6) * mm, "end": v(176.64, 23.6) * mm});
            skPoint(sketch, "E95.0.2.5", {"position": v(173.4, 20.34) * mm});
            skPoint(sketch, "E95.0.2.6", {"position": v(173.4, 20.34) * mm});
            skPoint(sketch, "E95.0.3.0", {"position": v(173.4, 28.27) * mm});
            skLineSegment(sketch, "E95.0.3.1", {"start": v(170.14, 25.02) * mm, "end": v(176.64, 25.02) * mm});
            skLineSegment(sketch, "E95.0.3.2", {"start": v(176.64, 31.52) * mm, "end": v(176.64, 25.02) * mm});
            skLineSegment(sketch, "E95.0.3.3", {"start": v(170.14, 31.52) * mm, "end": v(170.14, 25.02) * mm});
            skLineSegment(sketch, "E95.0.3.4", {"start": v(170.14, 31.52) * mm, "end": v(176.64, 31.52) * mm});
            skPoint(sketch, "E95.0.3.5", {"position": v(173.4, 28.27) * mm});
            skPoint(sketch, "E95.0.3.6", {"position": v(173.4, 28.27) * mm});
            skPoint(sketch, "E95.0.4.0", {"position": v(173.4, 36.19) * mm});
            skLineSegment(sketch, "E95.0.4.1", {"start": v(170.14, 32.94) * mm, "end": v(176.64, 32.94) * mm});
            skLineSegment(sketch, "E95.0.4.2", {"start": v(176.64, 39.44) * mm, "end": v(176.64, 32.94) * mm});
            skLineSegment(sketch, "E95.0.4.3", {"start": v(170.14, 39.44) * mm, "end": v(170.14, 32.94) * mm});
            skLineSegment(sketch, "E95.0.4.4", {"start": v(170.14, 39.44) * mm, "end": v(176.64, 39.44) * mm});
            skPoint(sketch, "E95.0.4.5", {"position": v(173.4, 36.19) * mm});
            skPoint(sketch, "E95.0.4.6", {"position": v(173.4, 36.19) * mm});
            skPoint(sketch, "E95.0.5.0", {"position": v(173.4, 44.11) * mm});
            skLineSegment(sketch, "E95.0.5.1", {"start": v(170.14, 40.86) * mm, "end": v(176.64, 40.86) * mm});
            skLineSegment(sketch, "E95.0.5.2", {"start": v(176.64, 47.36) * mm, "end": v(176.64, 40.86) * mm});
            skLineSegment(sketch, "E95.0.5.3", {"start": v(170.14, 47.36) * mm, "end": v(170.14, 40.86) * mm});
            skLineSegment(sketch, "E95.0.5.4", {"start": v(170.14, 47.36) * mm, "end": v(176.64, 47.36) * mm});
            skPoint(sketch, "E95.0.5.5", {"position": v(173.4, 44.11) * mm});
            skPoint(sketch, "E95.0.5.6", {"position": v(173.4, 44.11) * mm});
            skPoint(sketch, "E95.0.6.0", {"position": v(173.4, 52.03) * mm});
            skLineSegment(sketch, "E95.0.6.1", {"start": v(170.14, 48.78) * mm, "end": v(176.64, 48.78) * mm});
            skLineSegment(sketch, "E95.0.6.2", {"start": v(176.64, 55.28) * mm, "end": v(176.64, 48.78) * mm});
            skLineSegment(sketch, "E95.0.6.3", {"start": v(170.14, 55.28) * mm, "end": v(170.14, 48.78) * mm});
            skLineSegment(sketch, "E95.0.6.4", {"start": v(170.14, 55.28) * mm, "end": v(176.64, 55.28) * mm});
            skPoint(sketch, "E95.0.6.5", {"position": v(173.4, 52.03) * mm});
            skPoint(sketch, "E95.0.6.6", {"position": v(173.4, 52.03) * mm});
            skPoint(sketch, "E95.0.7.0", {"position": v(173.4, 59.96) * mm});
            skLineSegment(sketch, "E95.0.7.1", {"start": v(170.14, 56.7) * mm, "end": v(176.64, 56.7) * mm});
            skLineSegment(sketch, "E95.0.7.2", {"start": v(176.64, 63.2) * mm, "end": v(176.64, 56.7) * mm});
            skLineSegment(sketch, "E95.0.7.3", {"start": v(170.14, 63.2) * mm, "end": v(170.14, 56.7) * mm});
            skLineSegment(sketch, "E95.0.7.4", {"start": v(170.14, 63.2) * mm, "end": v(176.64, 63.2) * mm});
            skPoint(sketch, "E95.0.7.5", {"position": v(173.4, 59.96) * mm});
            skPoint(sketch, "E95.0.7.6", {"position": v(173.4, 59.96) * mm});
            skLineSegment(sketch, "E95.direction1", {"start": v(173.4, 4.5) * mm, "end": v(198.8, 4.5) * mm, "construction": true});
            skLineSegment(sketch, "E95.direction2", {"start": v(173.4, 4.5) * mm, "end": v(173.4, 12.42) * mm, "construction": true});
            skPoint(sketch, "E96", {"position": v(189.27, 4.27) * mm});
            skLineSegment(sketch, "E97.bottom", {"start": v(186.02, 7.52) * mm, "end": v(192.52, 7.52) * mm});
            skLineSegment(sketch, "E97.top", {"start": v(186.02, 1.02) * mm, "end": v(192.52, 1.02) * mm});
            skLineSegment(sketch, "E97.left", {"start": v(186.02, 7.52) * mm, "end": v(186.02, 1.02) * mm});
            skLineSegment(sketch, "E97.right", {"start": v(192.52, 7.52) * mm, "end": v(192.52, 1.02) * mm});
            skLineSegment(sketch, "E98.0.1.0", {"start": v(186.02, 15.5) * mm, "end": v(192.52, 15.5) * mm});
            skLineSegment(sketch, "E98.0.1.1", {"start": v(186.02, 15.5) * mm, "end": v(186.02, 9) * mm});
            skLineSegment(sketch, "E98.0.1.2", {"start": v(186.02, 9) * mm, "end": v(192.52, 9) * mm});
            skPoint(sketch, "E98.0.1.3", {"position": v(189.27, 12.25) * mm});
            skLineSegment(sketch, "E98.0.1.4", {"start": v(192.52, 15.5) * mm, "end": v(192.52, 9) * mm});
            skPoint(sketch, "E98.0.1.5", {"position": v(189.27, 12.25) * mm});
            skLineSegment(sketch, "E98.0.2.0", {"start": v(186.02, 23.48) * mm, "end": v(192.52, 23.48) * mm});
            skLineSegment(sketch, "E98.0.2.1", {"start": v(186.02, 23.48) * mm, "end": v(186.02, 16.98) * mm});
            skLineSegment(sketch, "E98.0.2.2", {"start": v(186.02, 16.98) * mm, "end": v(192.52, 16.98) * mm});
            skPoint(sketch, "E98.0.2.3", {"position": v(189.27, 20.23) * mm});
            skLineSegment(sketch, "E98.0.2.4", {"start": v(192.52, 23.48) * mm, "end": v(192.52, 16.98) * mm});
            skPoint(sketch, "E98.0.2.5", {"position": v(189.27, 20.23) * mm});
            skLineSegment(sketch, "E98.0.3.0", {"start": v(186.02, 31.47) * mm, "end": v(192.52, 31.47) * mm});
            skLineSegment(sketch, "E98.0.3.1", {"start": v(186.02, 31.47) * mm, "end": v(186.02, 24.97) * mm});
            skLineSegment(sketch, "E98.0.3.2", {"start": v(186.02, 24.97) * mm, "end": v(192.52, 24.97) * mm});
            skPoint(sketch, "E98.0.3.3", {"position": v(189.27, 28.22) * mm});
            skLineSegment(sketch, "E98.0.3.4", {"start": v(192.52, 31.47) * mm, "end": v(192.52, 24.97) * mm});
            skPoint(sketch, "E98.0.3.5", {"position": v(189.27, 28.22) * mm});
            skLineSegment(sketch, "E98.0.4.0", {"start": v(186.02, 39.45) * mm, "end": v(192.52, 39.45) * mm});
            skLineSegment(sketch, "E98.0.4.1", {"start": v(186.02, 39.45) * mm, "end": v(186.02, 32.95) * mm});
            skLineSegment(sketch, "E98.0.4.2", {"start": v(186.02, 32.95) * mm, "end": v(192.52, 32.95) * mm});
            skPoint(sketch, "E98.0.4.3", {"position": v(189.27, 36.2) * mm});
            skLineSegment(sketch, "E98.0.4.4", {"start": v(192.52, 39.45) * mm, "end": v(192.52, 32.95) * mm});
            skPoint(sketch, "E98.0.4.5", {"position": v(189.27, 36.2) * mm});
            skLineSegment(sketch, "E98.0.5.0", {"start": v(186.02, 47.43) * mm, "end": v(192.52, 47.43) * mm});
            skLineSegment(sketch, "E98.0.5.1", {"start": v(186.02, 47.43) * mm, "end": v(186.02, 40.93) * mm});
            skLineSegment(sketch, "E98.0.5.2", {"start": v(186.02, 40.93) * mm, "end": v(192.52, 40.93) * mm});
            skPoint(sketch, "E98.0.5.3", {"position": v(189.27, 44.18) * mm});
            skLineSegment(sketch, "E98.0.5.4", {"start": v(192.52, 47.43) * mm, "end": v(192.52, 40.93) * mm});
            skPoint(sketch, "E98.0.5.5", {"position": v(189.27, 44.18) * mm});
            skLineSegment(sketch, "E98.0.6.0", {"start": v(186.02, 55.42) * mm, "end": v(192.52, 55.42) * mm});
            skLineSegment(sketch, "E98.0.6.1", {"start": v(186.02, 55.42) * mm, "end": v(186.02, 48.92) * mm});
            skLineSegment(sketch, "E98.0.6.2", {"start": v(186.02, 48.92) * mm, "end": v(192.52, 48.92) * mm});
            skPoint(sketch, "E98.0.6.3", {"position": v(189.27, 52.17) * mm});
            skLineSegment(sketch, "E98.0.6.4", {"start": v(192.52, 55.42) * mm, "end": v(192.52, 48.92) * mm});
            skPoint(sketch, "E98.0.6.5", {"position": v(189.27, 52.17) * mm});
            skLineSegment(sketch, "E98.0.7.0", {"start": v(186.02, 63.4) * mm, "end": v(192.52, 63.4) * mm});
            skLineSegment(sketch, "E98.0.7.1", {"start": v(186.02, 63.4) * mm, "end": v(186.02, 56.9) * mm});
            skLineSegment(sketch, "E98.0.7.2", {"start": v(186.02, 56.9) * mm, "end": v(192.52, 56.9) * mm});
            skPoint(sketch, "E98.0.7.3", {"position": v(189.27, 60.15) * mm});
            skLineSegment(sketch, "E98.0.7.4", {"start": v(192.52, 63.4) * mm, "end": v(192.52, 56.9) * mm});
            skPoint(sketch, "E98.0.7.5", {"position": v(189.27, 60.15) * mm});
            skLineSegment(sketch, "E98.direction1", {"start": v(186.02, 7.52) * mm, "end": v(211.42, 7.52) * mm, "construction": true});
            skLineSegment(sketch, "E98.direction2", {"start": v(186.02, 7.52) * mm, "end": v(186.02, 15.5) * mm, "construction": true});
            skLineSegment(sketch, "E99.0.1.0", {"start": v(208.62, 15.3) * mm, "end": v(208.62, 8.8) * mm});
            skLineSegment(sketch, "E99.0.1.1", {"start": v(208.62, 8.8) * mm, "end": v(215.12, 8.8) * mm});
            skLineSegment(sketch, "E99.0.1.2", {"start": v(208.62, 15.3) * mm, "end": v(215.12, 15.3) * mm});
            skPoint(sketch, "E99.0.1.3", {"position": v(211.87, 12.04) * mm});
            skLineSegment(sketch, "E99.0.1.4", {"start": v(215.12, 15.3) * mm, "end": v(215.12, 8.8) * mm});
            skPoint(sketch, "E99.0.1.5", {"position": v(211.87, 12.04) * mm});
            skLineSegment(sketch, "E99.0.2.0", {"start": v(208.62, 23.4) * mm, "end": v(208.62, 16.9) * mm});
            skLineSegment(sketch, "E99.0.2.1", {"start": v(208.62, 16.9) * mm, "end": v(215.12, 16.9) * mm});
            skLineSegment(sketch, "E99.0.2.2", {"start": v(208.62, 23.4) * mm, "end": v(215.12, 23.4) * mm});
            skPoint(sketch, "E99.0.2.3", {"position": v(211.87, 20.15) * mm});
            skLineSegment(sketch, "E99.0.2.4", {"start": v(215.12, 23.4) * mm, "end": v(215.12, 16.9) * mm});
            skPoint(sketch, "E99.0.2.5", {"position": v(211.87, 20.15) * mm});
            skLineSegment(sketch, "E99.0.3.0", {"start": v(208.62, 31.51) * mm, "end": v(208.62, 25.01) * mm});
            skLineSegment(sketch, "E99.0.3.1", {"start": v(208.62, 25.01) * mm, "end": v(215.12, 25.01) * mm});
            skLineSegment(sketch, "E99.0.3.2", {"start": v(208.62, 31.51) * mm, "end": v(215.12, 31.51) * mm});
            skPoint(sketch, "E99.0.3.3", {"position": v(211.87, 28.26) * mm});
            skLineSegment(sketch, "E99.0.3.4", {"start": v(215.12, 31.51) * mm, "end": v(215.12, 25.01) * mm});
            skPoint(sketch, "E99.0.3.5", {"position": v(211.87, 28.26) * mm});
            skLineSegment(sketch, "E99.0.4.0", {"start": v(208.62, 39.62) * mm, "end": v(208.62, 33.12) * mm});
            skLineSegment(sketch, "E99.0.4.1", {"start": v(208.62, 33.12) * mm, "end": v(215.12, 33.12) * mm});
            skLineSegment(sketch, "E99.0.4.2", {"start": v(208.62, 39.62) * mm, "end": v(215.12, 39.62) * mm});
            skPoint(sketch, "E99.0.4.3", {"position": v(211.87, 36.37) * mm});
            skLineSegment(sketch, "E99.0.4.4", {"start": v(215.12, 39.62) * mm, "end": v(215.12, 33.12) * mm});
            skPoint(sketch, "E99.0.4.5", {"position": v(211.87, 36.37) * mm});
            skLineSegment(sketch, "E99.0.5.0", {"start": v(208.62, 47.74) * mm, "end": v(208.62, 41.24) * mm});
            skLineSegment(sketch, "E99.0.5.1", {"start": v(208.62, 41.24) * mm, "end": v(215.12, 41.24) * mm});
            skLineSegment(sketch, "E99.0.5.2", {"start": v(208.62, 47.74) * mm, "end": v(215.12, 47.74) * mm});
            skPoint(sketch, "E99.0.5.3", {"position": v(211.87, 44.49) * mm});
            skLineSegment(sketch, "E99.0.5.4", {"start": v(215.12, 47.74) * mm, "end": v(215.12, 41.24) * mm});
            skPoint(sketch, "E99.0.5.5", {"position": v(211.87, 44.49) * mm});
            skLineSegment(sketch, "E99.0.6.0", {"start": v(208.62, 55.85) * mm, "end": v(208.62, 49.35) * mm});
            skLineSegment(sketch, "E99.0.6.1", {"start": v(208.62, 49.35) * mm, "end": v(215.12, 49.35) * mm});
            skLineSegment(sketch, "E99.0.6.2", {"start": v(208.62, 55.85) * mm, "end": v(215.12, 55.85) * mm});
            skPoint(sketch, "E99.0.6.3", {"position": v(211.87, 52.6) * mm});
            skLineSegment(sketch, "E99.0.6.4", {"start": v(215.12, 55.85) * mm, "end": v(215.12, 49.35) * mm});
            skPoint(sketch, "E99.0.6.5", {"position": v(211.87, 52.6) * mm});
            skLineSegment(sketch, "E99.0.7.0", {"start": v(208.62, 63.96) * mm, "end": v(208.62, 57.46) * mm});
            skLineSegment(sketch, "E99.0.7.1", {"start": v(208.62, 57.46) * mm, "end": v(215.12, 57.46) * mm});
            skLineSegment(sketch, "E99.0.7.2", {"start": v(208.62, 63.96) * mm, "end": v(215.12, 63.96) * mm});
            skPoint(sketch, "E99.0.7.3", {"position": v(211.87, 60.7) * mm});
            skLineSegment(sketch, "E99.0.7.4", {"start": v(215.12, 63.96) * mm, "end": v(215.12, 57.46) * mm});
            skPoint(sketch, "E99.0.7.5", {"position": v(211.87, 60.7) * mm});
            skLineSegment(sketch, "E99.direction1", {"start": v(208.62, 0.68) * mm, "end": v(234.02, 0.68) * mm, "construction": true});
            skLineSegment(sketch, "E99.direction2", {"start": v(208.62, 0.68) * mm, "end": v(208.62, 8.8) * mm, "construction": true});
            skPoint(sketch, "E100.0.1.0", {"position": v(227.74, 11.87) * mm});
            skLineSegment(sketch, "E100.0.1.1", {"start": v(231, 15.12) * mm, "end": v(231, 8.62) * mm});
            skLineSegment(sketch, "E100.0.1.2", {"start": v(224.5, 15.12) * mm, "end": v(224.5, 8.62) * mm});
            skLineSegment(sketch, "E100.0.1.3", {"start": v(224.5, 15.12) * mm, "end": v(231, 15.12) * mm});
            skLineSegment(sketch, "E100.0.1.4", {"start": v(224.5, 8.62) * mm, "end": v(231, 8.62) * mm});
            skPoint(sketch, "E100.0.1.5", {"position": v(227.74, 11.87) * mm});
            skPoint(sketch, "E100.0.2.0", {"position": v(227.74, 20.04) * mm});
            skLineSegment(sketch, "E100.0.2.1", {"start": v(231, 23.3) * mm, "end": v(231, 16.8) * mm});
            skLineSegment(sketch, "E100.0.2.2", {"start": v(224.5, 23.3) * mm, "end": v(224.5, 16.8) * mm});
            skLineSegment(sketch, "E100.0.2.3", {"start": v(224.5, 23.3) * mm, "end": v(231, 23.3) * mm});
            skLineSegment(sketch, "E100.0.2.4", {"start": v(224.5, 16.8) * mm, "end": v(231, 16.8) * mm});
            skPoint(sketch, "E100.0.2.5", {"position": v(227.74, 20.04) * mm});
            skPoint(sketch, "E100.0.3.0", {"position": v(227.74, 28.21) * mm});
            skLineSegment(sketch, "E100.0.3.1", {"start": v(231, 31.46) * mm, "end": v(231, 24.96) * mm});
            skLineSegment(sketch, "E100.0.3.2", {"start": v(224.5, 31.46) * mm, "end": v(224.5, 24.96) * mm});
            skLineSegment(sketch, "E100.0.3.3", {"start": v(224.5, 31.46) * mm, "end": v(231, 31.46) * mm});
            skLineSegment(sketch, "E100.0.3.4", {"start": v(224.5, 24.96) * mm, "end": v(231, 24.96) * mm});
            skPoint(sketch, "E100.0.3.5", {"position": v(227.74, 28.21) * mm});
            skPoint(sketch, "E100.0.4.0", {"position": v(227.74, 36.39) * mm});
            skLineSegment(sketch, "E100.0.4.1", {"start": v(231, 39.64) * mm, "end": v(231, 33.14) * mm});
            skLineSegment(sketch, "E100.0.4.2", {"start": v(224.5, 39.64) * mm, "end": v(224.5, 33.14) * mm});
            skLineSegment(sketch, "E100.0.4.3", {"start": v(224.5, 39.64) * mm, "end": v(231, 39.64) * mm});
            skLineSegment(sketch, "E100.0.4.4", {"start": v(224.5, 33.14) * mm, "end": v(231, 33.14) * mm});
            skPoint(sketch, "E100.0.4.5", {"position": v(227.74, 36.39) * mm});
            skPoint(sketch, "E100.0.5.0", {"position": v(227.74, 44.56) * mm});
            skLineSegment(sketch, "E100.0.5.1", {"start": v(231, 47.8) * mm, "end": v(231, 41.3) * mm});
            skLineSegment(sketch, "E100.0.5.2", {"start": v(224.5, 47.8) * mm, "end": v(224.5, 41.3) * mm});
            skLineSegment(sketch, "E100.0.5.3", {"start": v(224.5, 47.8) * mm, "end": v(231, 47.8) * mm});
            skLineSegment(sketch, "E100.0.5.4", {"start": v(224.5, 41.3) * mm, "end": v(231, 41.3) * mm});
            skPoint(sketch, "E100.0.5.5", {"position": v(227.74, 44.56) * mm});
            skPoint(sketch, "E100.0.6.0", {"position": v(227.74, 52.73) * mm});
            skLineSegment(sketch, "E100.0.6.1", {"start": v(231, 55.98) * mm, "end": v(231, 49.48) * mm});
            skLineSegment(sketch, "E100.0.6.2", {"start": v(224.5, 55.98) * mm, "end": v(224.5, 49.48) * mm});
            skLineSegment(sketch, "E100.0.6.3", {"start": v(224.5, 55.98) * mm, "end": v(231, 55.98) * mm});
            skLineSegment(sketch, "E100.0.6.4", {"start": v(224.5, 49.48) * mm, "end": v(231, 49.48) * mm});
            skPoint(sketch, "E100.0.6.5", {"position": v(227.74, 52.73) * mm});
            skPoint(sketch, "E100.0.7.0", {"position": v(227.74, 60.9) * mm});
            skLineSegment(sketch, "E100.0.7.1", {"start": v(231, 64.15) * mm, "end": v(231, 57.65) * mm});
            skLineSegment(sketch, "E100.0.7.2", {"start": v(224.5, 64.15) * mm, "end": v(224.5, 57.65) * mm});
            skLineSegment(sketch, "E100.0.7.3", {"start": v(224.5, 64.15) * mm, "end": v(231, 64.15) * mm});
            skLineSegment(sketch, "E100.0.7.4", {"start": v(224.5, 57.65) * mm, "end": v(231, 57.65) * mm});
            skPoint(sketch, "E100.0.7.5", {"position": v(227.74, 60.9) * mm});
            skLineSegment(sketch, "E100.direction1", {"start": v(227.74, 3.7) * mm, "end": v(253.14, 3.7) * mm, "construction": true});
            skLineSegment(sketch, "E100.direction2", {"start": v(227.74, 3.7) * mm, "end": v(227.74, 11.87) * mm, "construction": true});
            skLineSegment(sketch, "E101.0.1.0", {"start": v(251.43, 14.94) * mm, "end": v(251.43, 8.44) * mm});
            skPoint(sketch, "E101.0.1.1", {"position": v(248.18, 11.69) * mm});
            skLineSegment(sketch, "E101.0.1.2", {"start": v(244.93, 14.94) * mm, "end": v(244.93, 8.44) * mm});
            skLineSegment(sketch, "E101.0.1.3", {"start": v(244.93, 8.44) * mm, "end": v(251.43, 8.44) * mm});
            skLineSegment(sketch, "E101.0.1.4", {"start": v(244.93, 14.94) * mm, "end": v(251.43, 14.94) * mm});
            skPoint(sketch, "E101.0.1.5", {"position": v(248.18, 11.69) * mm});
            skLineSegment(sketch, "E101.0.2.0", {"start": v(251.43, 23.23) * mm, "end": v(251.43, 16.73) * mm});
            skPoint(sketch, "E101.0.2.1", {"position": v(248.18, 19.98) * mm});
            skLineSegment(sketch, "E101.0.2.2", {"start": v(244.93, 23.23) * mm, "end": v(244.93, 16.73) * mm});
            skLineSegment(sketch, "E101.0.2.3", {"start": v(244.93, 16.73) * mm, "end": v(251.43, 16.73) * mm});
            skLineSegment(sketch, "E101.0.2.4", {"start": v(244.93, 23.23) * mm, "end": v(251.43, 23.23) * mm});
            skPoint(sketch, "E101.0.2.5", {"position": v(248.18, 19.98) * mm});
            skLineSegment(sketch, "E101.0.3.0", {"start": v(251.43, 31.51) * mm, "end": v(251.43, 25.01) * mm});
            skPoint(sketch, "E101.0.3.1", {"position": v(248.18, 28.26) * mm});
            skLineSegment(sketch, "E101.0.3.2", {"start": v(244.93, 31.51) * mm, "end": v(244.93, 25.01) * mm});
            skLineSegment(sketch, "E101.0.3.3", {"start": v(244.93, 25.01) * mm, "end": v(251.43, 25.01) * mm});
            skLineSegment(sketch, "E101.0.3.4", {"start": v(244.93, 31.51) * mm, "end": v(251.43, 31.51) * mm});
            skPoint(sketch, "E101.0.3.5", {"position": v(248.18, 28.26) * mm});
            skLineSegment(sketch, "E101.0.4.0", {"start": v(251.43, 39.8) * mm, "end": v(251.43, 33.3) * mm});
            skPoint(sketch, "E101.0.4.1", {"position": v(248.18, 36.55) * mm});
            skLineSegment(sketch, "E101.0.4.2", {"start": v(244.93, 39.8) * mm, "end": v(244.93, 33.3) * mm});
            skLineSegment(sketch, "E101.0.4.3", {"start": v(244.93, 33.3) * mm, "end": v(251.43, 33.3) * mm});
            skLineSegment(sketch, "E101.0.4.4", {"start": v(244.93, 39.8) * mm, "end": v(251.43, 39.8) * mm});
            skPoint(sketch, "E101.0.4.5", {"position": v(248.18, 36.55) * mm});
            skLineSegment(sketch, "E101.0.5.0", {"start": v(251.43, 48.1) * mm, "end": v(251.43, 41.6) * mm});
            skPoint(sketch, "E101.0.5.1", {"position": v(248.18, 44.84) * mm});
            skLineSegment(sketch, "E101.0.5.2", {"start": v(244.93, 48.1) * mm, "end": v(244.93, 41.6) * mm});
            skLineSegment(sketch, "E101.0.5.3", {"start": v(244.93, 41.6) * mm, "end": v(251.43, 41.6) * mm});
            skLineSegment(sketch, "E101.0.5.4", {"start": v(244.93, 48.1) * mm, "end": v(251.43, 48.1) * mm});
            skPoint(sketch, "E101.0.5.5", {"position": v(248.18, 44.84) * mm});
            skLineSegment(sketch, "E101.0.6.0", {"start": v(251.43, 56.38) * mm, "end": v(251.43, 49.88) * mm});
            skPoint(sketch, "E101.0.6.1", {"position": v(248.18, 53.13) * mm});
            skLineSegment(sketch, "E101.0.6.2", {"start": v(244.93, 56.38) * mm, "end": v(244.93, 49.88) * mm});
            skLineSegment(sketch, "E101.0.6.3", {"start": v(244.93, 49.88) * mm, "end": v(251.43, 49.88) * mm});
            skLineSegment(sketch, "E101.0.6.4", {"start": v(244.93, 56.38) * mm, "end": v(251.43, 56.38) * mm});
            skPoint(sketch, "E101.0.6.5", {"position": v(248.18, 53.13) * mm});
            skLineSegment(sketch, "E101.0.7.0", {"start": v(251.43, 64.67) * mm, "end": v(251.43, 58.17) * mm});
            skPoint(sketch, "E101.0.7.1", {"position": v(248.18, 61.42) * mm});
            skLineSegment(sketch, "E101.0.7.2", {"start": v(244.93, 64.67) * mm, "end": v(244.93, 58.17) * mm});
            skLineSegment(sketch, "E101.0.7.3", {"start": v(244.93, 58.17) * mm, "end": v(251.43, 58.17) * mm});
            skLineSegment(sketch, "E101.0.7.4", {"start": v(244.93, 64.67) * mm, "end": v(251.43, 64.67) * mm});
            skPoint(sketch, "E101.0.7.5", {"position": v(248.18, 61.42) * mm});
            skLineSegment(sketch, "E101.direction1", {"start": v(251.43, 0.15) * mm, "end": v(276.83, 0.15) * mm, "construction": true});
            skLineSegment(sketch, "E101.direction2", {"start": v(251.43, 0.15) * mm, "end": v(251.43, 8.44) * mm, "construction": true});
            skLineSegment(sketch, "E102.0.1.0", {"start": v(260.8, 14.77) * mm, "end": v(260.8, 8.27) * mm});
            skLineSegment(sketch, "E102.0.1.1", {"start": v(267.3, 14.77) * mm, "end": v(267.3, 8.27) * mm});
            skLineSegment(sketch, "E102.0.1.2", {"start": v(260.8, 14.77) * mm, "end": v(267.3, 14.77) * mm});
            skLineSegment(sketch, "E102.0.1.3", {"start": v(260.8, 8.27) * mm, "end": v(267.3, 8.27) * mm});
            skPoint(sketch, "E102.0.1.4", {"position": v(264.05, 11.52) * mm});
            skPoint(sketch, "E102.0.1.5", {"position": v(264.05, 11.52) * mm});
            skLineSegment(sketch, "E102.0.2.0", {"start": v(260.8, 23.11) * mm, "end": v(260.8, 16.61) * mm});
            skLineSegment(sketch, "E102.0.2.1", {"start": v(267.3, 23.11) * mm, "end": v(267.3, 16.61) * mm});
            skLineSegment(sketch, "E102.0.2.2", {"start": v(260.8, 23.11) * mm, "end": v(267.3, 23.11) * mm});
            skLineSegment(sketch, "E102.0.2.3", {"start": v(260.8, 16.61) * mm, "end": v(267.3, 16.61) * mm});
            skPoint(sketch, "E102.0.2.4", {"position": v(264.05, 19.86) * mm});
            skPoint(sketch, "E102.0.2.5", {"position": v(264.05, 19.86) * mm});
            skLineSegment(sketch, "E102.0.3.0", {"start": v(260.8, 31.46) * mm, "end": v(260.8, 24.96) * mm});
            skLineSegment(sketch, "E102.0.3.1", {"start": v(267.3, 31.46) * mm, "end": v(267.3, 24.96) * mm});
            skLineSegment(sketch, "E102.0.3.2", {"start": v(260.8, 31.46) * mm, "end": v(267.3, 31.46) * mm});
            skLineSegment(sketch, "E102.0.3.3", {"start": v(260.8, 24.96) * mm, "end": v(267.3, 24.96) * mm});
            skPoint(sketch, "E102.0.3.4", {"position": v(264.05, 28.21) * mm});
            skPoint(sketch, "E102.0.3.5", {"position": v(264.05, 28.21) * mm});
            skLineSegment(sketch, "E102.0.4.0", {"start": v(260.8, 39.81) * mm, "end": v(260.8, 33.31) * mm});
            skLineSegment(sketch, "E102.0.4.1", {"start": v(267.3, 39.81) * mm, "end": v(267.3, 33.31) * mm});
            skLineSegment(sketch, "E102.0.4.2", {"start": v(260.8, 39.81) * mm, "end": v(267.3, 39.81) * mm});
            skLineSegment(sketch, "E102.0.4.3", {"start": v(260.8, 33.31) * mm, "end": v(267.3, 33.31) * mm});
            skPoint(sketch, "E102.0.4.4", {"position": v(264.05, 36.56) * mm});
            skPoint(sketch, "E102.0.4.5", {"position": v(264.05, 36.56) * mm});
            skLineSegment(sketch, "E102.0.5.0", {"start": v(260.8, 48.16) * mm, "end": v(260.8, 41.66) * mm});
            skLineSegment(sketch, "E102.0.5.1", {"start": v(267.3, 48.16) * mm, "end": v(267.3, 41.66) * mm});
            skLineSegment(sketch, "E102.0.5.2", {"start": v(260.8, 48.16) * mm, "end": v(267.3, 48.16) * mm});
            skLineSegment(sketch, "E102.0.5.3", {"start": v(260.8, 41.66) * mm, "end": v(267.3, 41.66) * mm});
            skPoint(sketch, "E102.0.5.4", {"position": v(264.05, 44.91) * mm});
            skPoint(sketch, "E102.0.5.5", {"position": v(264.05, 44.91) * mm});
            skLineSegment(sketch, "E102.0.6.0", {"start": v(260.8, 56.51) * mm, "end": v(260.8, 50.01) * mm});
            skLineSegment(sketch, "E102.0.6.1", {"start": v(267.3, 56.51) * mm, "end": v(267.3, 50.01) * mm});
            skLineSegment(sketch, "E102.0.6.2", {"start": v(260.8, 56.51) * mm, "end": v(267.3, 56.51) * mm});
            skLineSegment(sketch, "E102.0.6.3", {"start": v(260.8, 50.01) * mm, "end": v(267.3, 50.01) * mm});
            skPoint(sketch, "E102.0.6.4", {"position": v(264.05, 53.26) * mm});
            skPoint(sketch, "E102.0.6.5", {"position": v(264.05, 53.26) * mm});
            skLineSegment(sketch, "E102.0.7.0", {"start": v(260.8, 64.86) * mm, "end": v(260.8, 58.36) * mm});
            skLineSegment(sketch, "E102.0.7.1", {"start": v(267.3, 64.86) * mm, "end": v(267.3, 58.36) * mm});
            skLineSegment(sketch, "E102.0.7.2", {"start": v(260.8, 64.86) * mm, "end": v(267.3, 64.86) * mm});
            skLineSegment(sketch, "E102.0.7.3", {"start": v(260.8, 58.36) * mm, "end": v(267.3, 58.36) * mm});
            skPoint(sketch, "E102.0.7.4", {"position": v(264.05, 61.6) * mm});
            skPoint(sketch, "E102.0.7.5", {"position": v(264.05, 61.6) * mm});
            skLineSegment(sketch, "E102.direction1", {"start": v(260.8, -0.08) * mm, "end": v(286.2, -0.08) * mm, "construction": true});
            skLineSegment(sketch, "E102.direction2", {"start": v(260.8, -0.08) * mm, "end": v(260.8, 8.27) * mm, "construction": true});
            skLineSegment(sketch, "E103.0.1.0", {"start": v(279.2, 8.1) * mm, "end": v(285.7, 8.1) * mm});
            skLineSegment(sketch, "E103.0.1.1", {"start": v(279.2, 14.6) * mm, "end": v(279.2, 8.1) * mm});
            skLineSegment(sketch, "E103.0.1.2", {"start": v(279.2, 14.6) * mm, "end": v(285.7, 14.6) * mm});
            skLineSegment(sketch, "E103.0.1.3", {"start": v(285.7, 14.6) * mm, "end": v(285.7, 8.1) * mm});
            skPoint(sketch, "E103.0.1.4", {"position": v(282.45, 11.35) * mm});
            skPoint(sketch, "E103.0.1.5", {"position": v(282.45, 11.35) * mm});
            skLineSegment(sketch, "E103.0.2.0", {"start": v(279.2, 16.56) * mm, "end": v(285.7, 16.56) * mm});
            skLineSegment(sketch, "E103.0.2.1", {"start": v(279.2, 23.06) * mm, "end": v(279.2, 16.56) * mm});
            skLineSegment(sketch, "E103.0.2.2", {"start": v(279.2, 23.06) * mm, "end": v(285.7, 23.06) * mm});
            skLineSegment(sketch, "E103.0.2.3", {"start": v(285.7, 23.06) * mm, "end": v(285.7, 16.56) * mm});
            skPoint(sketch, "E103.0.2.4", {"position": v(282.45, 19.8) * mm});
            skPoint(sketch, "E103.0.2.5", {"position": v(282.45, 19.8) * mm});
            skLineSegment(sketch, "E103.0.3.0", {"start": v(279.2, 25.01) * mm, "end": v(285.7, 25.01) * mm});
            skLineSegment(sketch, "E103.0.3.1", {"start": v(279.2, 31.51) * mm, "end": v(279.2, 25.01) * mm});
            skLineSegment(sketch, "E103.0.3.2", {"start": v(279.2, 31.51) * mm, "end": v(285.7, 31.51) * mm});
            skLineSegment(sketch, "E103.0.3.3", {"start": v(285.7, 31.51) * mm, "end": v(285.7, 25.01) * mm});
            skPoint(sketch, "E103.0.3.4", {"position": v(282.45, 28.26) * mm});
            skPoint(sketch, "E103.0.3.5", {"position": v(282.45, 28.26) * mm});
            skLineSegment(sketch, "E103.0.4.0", {"start": v(279.2, 33.47) * mm, "end": v(285.7, 33.47) * mm});
            skLineSegment(sketch, "E103.0.4.1", {"start": v(279.2, 39.97) * mm, "end": v(279.2, 33.47) * mm});
            skLineSegment(sketch, "E103.0.4.2", {"start": v(279.2, 39.97) * mm, "end": v(285.7, 39.97) * mm});
            skLineSegment(sketch, "E103.0.4.3", {"start": v(285.7, 39.97) * mm, "end": v(285.7, 33.47) * mm});
            skPoint(sketch, "E103.0.4.4", {"position": v(282.45, 36.72) * mm});
            skPoint(sketch, "E103.0.4.5", {"position": v(282.45, 36.72) * mm});
            skLineSegment(sketch, "E103.0.5.0", {"start": v(279.2, 41.92) * mm, "end": v(285.7, 41.92) * mm});
            skLineSegment(sketch, "E103.0.5.1", {"start": v(279.2, 48.42) * mm, "end": v(279.2, 41.92) * mm});
            skLineSegment(sketch, "E103.0.5.2", {"start": v(279.2, 48.42) * mm, "end": v(285.7, 48.42) * mm});
            skLineSegment(sketch, "E103.0.5.3", {"start": v(285.7, 48.42) * mm, "end": v(285.7, 41.92) * mm});
            skPoint(sketch, "E103.0.5.4", {"position": v(282.45, 45.17) * mm});
            skPoint(sketch, "E103.0.5.5", {"position": v(282.45, 45.17) * mm});
            skLineSegment(sketch, "E103.0.6.0", {"start": v(279.2, 50.38) * mm, "end": v(285.7, 50.38) * mm});
            skLineSegment(sketch, "E103.0.6.1", {"start": v(279.2, 56.88) * mm, "end": v(279.2, 50.38) * mm});
            skLineSegment(sketch, "E103.0.6.2", {"start": v(279.2, 56.88) * mm, "end": v(285.7, 56.88) * mm});
            skLineSegment(sketch, "E103.0.6.3", {"start": v(285.7, 56.88) * mm, "end": v(285.7, 50.38) * mm});
            skPoint(sketch, "E103.0.6.4", {"position": v(282.45, 53.63) * mm});
            skPoint(sketch, "E103.0.6.5", {"position": v(282.45, 53.63) * mm});
            skLineSegment(sketch, "E103.0.7.0", {"start": v(279.2, 58.84) * mm, "end": v(285.7, 58.84) * mm});
            skLineSegment(sketch, "E103.0.7.1", {"start": v(279.2, 65.34) * mm, "end": v(279.2, 58.84) * mm});
            skLineSegment(sketch, "E103.0.7.2", {"start": v(279.2, 65.34) * mm, "end": v(285.7, 65.34) * mm});
            skLineSegment(sketch, "E103.0.7.3", {"start": v(285.7, 65.34) * mm, "end": v(285.7, 58.84) * mm});
            skPoint(sketch, "E103.0.7.4", {"position": v(282.45, 62.09) * mm});
            skPoint(sketch, "E103.0.7.5", {"position": v(282.45, 62.09) * mm});
            skLineSegment(sketch, "E103.direction1", {"start": v(279.2, -0.35) * mm, "end": v(304.6, -0.35) * mm, "construction": true});
            skLineSegment(sketch, "E103.direction2", {"start": v(279.2, -0.35) * mm, "end": v(279.2, 8.1) * mm, "construction": true});
            skPoint(sketch, "E104.0.1.0", {"position": v(298.33, 11.18) * mm});
            skLineSegment(sketch, "E104.0.1.1", {"start": v(295.08, 7.93) * mm, "end": v(301.58, 7.93) * mm});
            skLineSegment(sketch, "E104.0.1.2", {"start": v(295.08, 14.43) * mm, "end": v(301.58, 14.43) * mm});
            skPoint(sketch, "E104.0.1.3", {"position": v(304.8, 2.55) * mm});
            skLineSegment(sketch, "E104.0.1.4", {"start": v(295.08, 14.43) * mm, "end": v(295.08, 7.93) * mm});
            skLineSegment(sketch, "E104.0.1.5", {"start": v(301.58, 14.43) * mm, "end": v(301.58, 7.93) * mm});
            skPoint(sketch, "E104.0.1.6", {"position": v(298.33, 11.18) * mm});
            skPoint(sketch, "E104.0.2.0", {"position": v(298.33, 19.7) * mm});
            skLineSegment(sketch, "E104.0.2.1", {"start": v(295.08, 16.45) * mm, "end": v(301.58, 16.45) * mm});
            skLineSegment(sketch, "E104.0.2.2", {"start": v(295.08, 22.95) * mm, "end": v(301.58, 22.95) * mm});
            skPoint(sketch, "E104.0.2.3", {"position": v(304.8, 11.06) * mm});
            skLineSegment(sketch, "E104.0.2.4", {"start": v(295.08, 22.95) * mm, "end": v(295.08, 16.45) * mm});
            skLineSegment(sketch, "E104.0.2.5", {"start": v(301.58, 22.95) * mm, "end": v(301.58, 16.45) * mm});
            skPoint(sketch, "E104.0.2.6", {"position": v(298.33, 19.7) * mm});
            skPoint(sketch, "E104.0.3.0", {"position": v(298.33, 28.22) * mm});
            skLineSegment(sketch, "E104.0.3.1", {"start": v(295.08, 24.97) * mm, "end": v(301.58, 24.97) * mm});
            skLineSegment(sketch, "E104.0.3.2", {"start": v(295.08, 31.47) * mm, "end": v(301.58, 31.47) * mm});
            skPoint(sketch, "E104.0.3.3", {"position": v(304.8, 19.58) * mm});
            skLineSegment(sketch, "E104.0.3.4", {"start": v(295.08, 31.47) * mm, "end": v(295.08, 24.97) * mm});
            skLineSegment(sketch, "E104.0.3.5", {"start": v(301.58, 31.47) * mm, "end": v(301.58, 24.97) * mm});
            skPoint(sketch, "E104.0.3.6", {"position": v(298.33, 28.22) * mm});
            skPoint(sketch, "E104.0.4.0", {"position": v(298.33, 36.74) * mm});
            skLineSegment(sketch, "E104.0.4.1", {"start": v(295.08, 33.49) * mm, "end": v(301.58, 33.49) * mm});
            skLineSegment(sketch, "E104.0.4.2", {"start": v(295.08, 39.99) * mm, "end": v(301.58, 39.99) * mm});
            skPoint(sketch, "E104.0.4.3", {"position": v(304.8, 28.1) * mm});
            skLineSegment(sketch, "E104.0.4.4", {"start": v(295.08, 39.99) * mm, "end": v(295.08, 33.49) * mm});
            skLineSegment(sketch, "E104.0.4.5", {"start": v(301.58, 39.99) * mm, "end": v(301.58, 33.49) * mm});
            skPoint(sketch, "E104.0.4.6", {"position": v(298.33, 36.74) * mm});
            skPoint(sketch, "E104.0.5.0", {"position": v(298.33, 45.26) * mm});
            skLineSegment(sketch, "E104.0.5.1", {"start": v(295.08, 42) * mm, "end": v(301.58, 42) * mm});
            skLineSegment(sketch, "E104.0.5.2", {"start": v(295.08, 48.5) * mm, "end": v(301.58, 48.5) * mm});
            skPoint(sketch, "E104.0.5.3", {"position": v(304.8, 36.62) * mm});
            skLineSegment(sketch, "E104.0.5.4", {"start": v(295.08, 48.5) * mm, "end": v(295.08, 42) * mm});
            skLineSegment(sketch, "E104.0.5.5", {"start": v(301.58, 48.5) * mm, "end": v(301.58, 42) * mm});
            skPoint(sketch, "E104.0.5.6", {"position": v(298.33, 45.26) * mm});
            skPoint(sketch, "E104.0.6.0", {"position": v(298.33, 53.78) * mm});
            skLineSegment(sketch, "E104.0.6.1", {"start": v(295.08, 50.53) * mm, "end": v(301.58, 50.53) * mm});
            skLineSegment(sketch, "E104.0.6.2", {"start": v(295.08, 57.03) * mm, "end": v(301.58, 57.03) * mm});
            skPoint(sketch, "E104.0.6.3", {"position": v(304.8, 45.14) * mm});
            skLineSegment(sketch, "E104.0.6.4", {"start": v(295.08, 57.03) * mm, "end": v(295.08, 50.53) * mm});
            skLineSegment(sketch, "E104.0.6.5", {"start": v(301.58, 57.03) * mm, "end": v(301.58, 50.53) * mm});
            skPoint(sketch, "E104.0.6.6", {"position": v(298.33, 53.78) * mm});
            skPoint(sketch, "E104.0.7.0", {"position": v(298.33, 62.3) * mm});
            skLineSegment(sketch, "E104.0.7.1", {"start": v(295.08, 59.05) * mm, "end": v(301.58, 59.05) * mm});
            skLineSegment(sketch, "E104.0.7.2", {"start": v(295.08, 65.55) * mm, "end": v(301.58, 65.55) * mm});
            skPoint(sketch, "E104.0.7.3", {"position": v(304.8, 53.66) * mm});
            skLineSegment(sketch, "E104.0.7.4", {"start": v(295.08, 65.55) * mm, "end": v(295.08, 59.05) * mm});
            skLineSegment(sketch, "E104.0.7.5", {"start": v(301.58, 65.55) * mm, "end": v(301.58, 59.05) * mm});
            skPoint(sketch, "E104.0.7.6", {"position": v(298.33, 62.3) * mm});
            skLineSegment(sketch, "E104.direction1", {"start": v(298.33, 2.66) * mm, "end": v(323.73, 2.66) * mm, "construction": true});
            skLineSegment(sketch, "E104.direction2", {"start": v(298.33, 2.66) * mm, "end": v(298.33, 11.18) * mm, "construction": true});
            skPoint(sketch, "E105", {"position": v(11.11, 21.1) * mm});
            skPoint(sketch, "E106.0.1.0", {"position": v(11.11, 13.98) * mm});
            skPoint(sketch, "E106.0.1.1", {"position": v(11.11, 28.19) * mm});
            skLineSegment(sketch, "E106.0.1.2", {"start": v(7.86, 17.23) * mm, "end": v(7.86, 10.73) * mm});
            skLineSegment(sketch, "E106.0.1.3", {"start": v(7.86, 17.23) * mm, "end": v(14.36, 17.23) * mm});
            skLineSegment(sketch, "E106.0.1.4", {"start": v(7.86, 10.73) * mm, "end": v(14.36, 10.73) * mm});
            skLineSegment(sketch, "E106.0.1.5", {"start": v(14.36, 17.23) * mm, "end": v(14.36, 10.73) * mm});
            skPoint(sketch, "E106.0.1.6", {"position": v(11.11, 13.98) * mm});
            skPoint(sketch, "E106.0.1.7", {"position": v(11.11, 13.98) * mm});
            skPoint(sketch, "E106.0.2.0", {"position": v(11.11, 21.08) * mm});
            skPoint(sketch, "E106.0.2.1", {"position": v(11.11, 35.29) * mm});
            skLineSegment(sketch, "E106.0.2.2", {"start": v(7.86, 24.33) * mm, "end": v(7.86, 17.83) * mm});
            skLineSegment(sketch, "E106.0.2.3", {"start": v(7.86, 24.33) * mm, "end": v(14.36, 24.33) * mm});
            skLineSegment(sketch, "E106.0.2.4", {"start": v(7.86, 17.83) * mm, "end": v(14.36, 17.83) * mm});
            skLineSegment(sketch, "E106.0.2.5", {"start": v(14.36, 24.33) * mm, "end": v(14.36, 17.83) * mm});
            skPoint(sketch, "E106.0.2.6", {"position": v(11.11, 21.08) * mm});
            skPoint(sketch, "E106.0.2.7", {"position": v(11.11, 21.08) * mm});
            skPoint(sketch, "E106.0.3.0", {"position": v(11.11, 28.18) * mm});
            skPoint(sketch, "E106.0.3.1", {"position": v(11.11, 42.38) * mm});
            skLineSegment(sketch, "E106.0.3.2", {"start": v(7.86, 31.43) * mm, "end": v(7.86, 24.93) * mm});
            skLineSegment(sketch, "E106.0.3.3", {"start": v(7.86, 31.43) * mm, "end": v(14.36, 31.43) * mm});
            skLineSegment(sketch, "E106.0.3.4", {"start": v(7.86, 24.93) * mm, "end": v(14.36, 24.93) * mm});
            skLineSegment(sketch, "E106.0.3.5", {"start": v(14.36, 31.43) * mm, "end": v(14.36, 24.93) * mm});
            skPoint(sketch, "E106.0.3.6", {"position": v(11.11, 28.18) * mm});
            skPoint(sketch, "E106.0.3.7", {"position": v(11.11, 28.18) * mm});
            skPoint(sketch, "E106.0.4.0", {"position": v(11.11, 35.27) * mm});
            skPoint(sketch, "E106.0.4.1", {"position": v(11.11, 49.48) * mm});
            skLineSegment(sketch, "E106.0.4.2", {"start": v(7.86, 38.52) * mm, "end": v(7.86, 32.02) * mm});
            skLineSegment(sketch, "E106.0.4.3", {"start": v(7.86, 38.52) * mm, "end": v(14.36, 38.52) * mm});
            skLineSegment(sketch, "E106.0.4.4", {"start": v(7.86, 32.02) * mm, "end": v(14.36, 32.02) * mm});
            skLineSegment(sketch, "E106.0.4.5", {"start": v(14.36, 38.52) * mm, "end": v(14.36, 32.02) * mm});
            skPoint(sketch, "E106.0.4.6", {"position": v(11.11, 35.27) * mm});
            skPoint(sketch, "E106.0.4.7", {"position": v(11.11, 35.27) * mm});
            skPoint(sketch, "E106.0.5.0", {"position": v(11.11, 42.37) * mm});
            skPoint(sketch, "E106.0.5.1", {"position": v(11.11, 56.58) * mm});
            skLineSegment(sketch, "E106.0.5.2", {"start": v(7.86, 45.62) * mm, "end": v(7.86, 39.12) * mm});
            skLineSegment(sketch, "E106.0.5.3", {"start": v(7.86, 45.62) * mm, "end": v(14.36, 45.62) * mm});
            skLineSegment(sketch, "E106.0.5.4", {"start": v(7.86, 39.12) * mm, "end": v(14.36, 39.12) * mm});
            skLineSegment(sketch, "E106.0.5.5", {"start": v(14.36, 45.62) * mm, "end": v(14.36, 39.12) * mm});
            skPoint(sketch, "E106.0.5.6", {"position": v(11.11, 42.37) * mm});
            skPoint(sketch, "E106.0.5.7", {"position": v(11.11, 42.37) * mm});
            skPoint(sketch, "E106.0.6.0", {"position": v(11.11, 49.47) * mm});
            skPoint(sketch, "E106.0.6.1", {"position": v(11.11, 63.67) * mm});
            skLineSegment(sketch, "E106.0.6.2", {"start": v(7.86, 52.72) * mm, "end": v(7.86, 46.22) * mm});
            skLineSegment(sketch, "E106.0.6.3", {"start": v(7.86, 52.72) * mm, "end": v(14.36, 52.72) * mm});
            skLineSegment(sketch, "E106.0.6.4", {"start": v(7.86, 46.22) * mm, "end": v(14.36, 46.22) * mm});
            skLineSegment(sketch, "E106.0.6.5", {"start": v(14.36, 52.72) * mm, "end": v(14.36, 46.22) * mm});
            skPoint(sketch, "E106.0.6.6", {"position": v(11.11, 49.47) * mm});
            skPoint(sketch, "E106.0.6.7", {"position": v(11.11, 49.47) * mm});
            skPoint(sketch, "E106.0.7.0", {"position": v(11.11, 56.56) * mm});
            skPoint(sketch, "E106.0.7.1", {"position": v(11.11, 70.77) * mm});
            skLineSegment(sketch, "E106.0.7.2", {"start": v(7.86, 59.81) * mm, "end": v(7.86, 53.31) * mm});
            skLineSegment(sketch, "E106.0.7.3", {"start": v(7.86, 59.81) * mm, "end": v(14.36, 59.81) * mm});
            skLineSegment(sketch, "E106.0.7.4", {"start": v(7.86, 53.31) * mm, "end": v(14.36, 53.31) * mm});
            skLineSegment(sketch, "E106.0.7.5", {"start": v(14.36, 59.81) * mm, "end": v(14.36, 53.31) * mm});
            skPoint(sketch, "E106.0.7.6", {"position": v(11.11, 56.56) * mm});
            skPoint(sketch, "E106.0.7.7", {"position": v(11.11, 56.56) * mm});
            skLineSegment(sketch, "E106.direction1", {"start": v(11.11, 6.89) * mm, "end": v(36.11, 6.89) * mm, "construction": true});
            skLineSegment(sketch, "E106.direction2", {"start": v(11.11, 6.89) * mm, "end": v(11.11, 13.98) * mm, "construction": true});
            skLineSegment(sketch, "E107", {"start": v(345.34, -11.78) * mm, "end": v(345.34, 72.6) * mm, "construction": true});
            skLineSegment(sketch, "E108", {"start": v(374.16, -13.41) * mm, "end": v(374.16, 70.78) * mm, "construction": true});
            skLineSegment(sketch, "E109", {"start": v(401.36, -15.95) * mm, "end": v(401.36, 71.14) * mm, "construction": true});
            skLineSegment(sketch, "E110", {"start": v(427.04, -15.77) * mm, "end": v(427.04, 70.78) * mm, "construction": true});
            skLineSegment(sketch, "E111", {"start": v(474.15, -18.13) * mm, "end": v(474.15, 73.32) * mm, "construction": true});
            skLineSegment(sketch, "E112", {"start": v(314.8, -23.18) * mm, "end": v(314.8, 74.56) * mm, "construction": true});
            skPoint(sketch, "E113", {"position": v(314.8, 19.6) * mm});
            skPoint(sketch, "E114", {"position": v(330.68, 19.53) * mm});
            skPoint(sketch, "E115", {"position": v(345.34, 19.45) * mm});
            skPoint(sketch, "E116", {"position": v(361.21, 19.38) * mm});
            skPoint(sketch, "E117", {"position": v(374.16, 19.31) * mm});
            skPoint(sketch, "E118", {"position": v(390.03, 19.23) * mm});
            skPoint(sketch, "E119", {"position": v(390.06, 5.7) * mm});
            skPoint(sketch, "E120", {"position": v(401.36, 19.18) * mm});
            skPoint(sketch, "E121", {"position": v(417.24, 19.1) * mm});
            skPoint(sketch, "E122", {"position": v(417.22, 5.44) * mm});
            skLineSegment(sketch, "E123", {"start": v(617.23, -23.82) * mm, "end": v(617.23, 80.23) * mm, "construction": true});
            skSolve(sketch);
        }
        {
            var Q0;
            Q0=qSketchRegion(id+"F0",true);
            extrude(context, id + "F1", {"entities" : qUnion([Q0]), "depth" : 1.52 * mm});
        }
        {
            var Q0;
            Q0=makeQuery(id+"F1.opExtrude","CAP_FACE",FACE,{"disambiguationData":[OSD([sQuery(id+"F0.wireOp",EDGE,"E0"),sQuery(id+"F0.wireOp",EDGE,"E1"),sQuery(id+"F0.wireOp",EDGE,"E2"),sQuery(id+"F0.wireOp",EDGE,"E3")])],"isStart":false});
            var sketch = newSketch(context, id + "F2", { "sketchPlane" : qUnion([Q0])});
            skLineSegment(sketch, "E124", {"start": v(0, 28.2) * mm, "end": v(635, 28.2) * mm, "construction": true});
            skSolve(sketch);
        }
        {
            var Q0;
            Q0=makeQuery(id+"F2.imprint","IMPRINT",FACE,{"disambiguationData":[TD([[makeQuery(id+"F2.imprint","IMPRINT",EDGE,{"derivedFrom":makeQuery(id+"F1.opExtrude","CAP_EDGE",EDGE,{"disambiguationData":[OSD([sQuery(id+"F0.wireOp",EDGE,"E0")])],"isStart":false})}),-1.0]])]});
            var sketch = newSketch(context, id + "F3", { "sketchPlane" : qUnion([Q0])});
            skCircle(sketch, "E125", {"center": v(97.4, 23.14) * mm, "radius": 1.13 * mm});
            skLineSegment(sketch, "E126", {"start": v(0, 22.22) * mm, "end": v(635, 28.2) * mm, "construction": true});
            skCircle(sketch, "E127", {"center": v(3.18, 22.25) * mm, "radius": 1.13 * mm});
            skCircle(sketch, "E128", {"center": v(181.33, 23.93) * mm, "radius": 1.13 * mm});
            skCircle(sketch, "E129", {"center": v(290.4, 24.95) * mm, "radius": 1.13 * mm});
            skCircle(sketch, "E130", {"center": v(409.3, 26.07) * mm, "radius": 1.13 * mm});
            skCircle(sketch, "E131", {"center": v(524.06, 27.15) * mm, "radius": 1.13 * mm});
            skCircle(sketch, "E132", {"center": v(624.44, 28.1) * mm, "radius": 1.13 * mm});
            skCircle(sketch, "E133.MirrorC", {"center": v(97.4, 33.25) * mm, "radius": 1.13 * mm});
            skCircle(sketch, "E134.MirrorC", {"center": v(3.18, 34.14) * mm, "radius": 1.13 * mm});
            skCircle(sketch, "E135.MirrorC", {"center": v(181.33, 32.46) * mm, "radius": 1.13 * mm});
            skCircle(sketch, "E136.MirrorC", {"center": v(290.4, 31.44) * mm, "radius": 1.13 * mm});
            skCircle(sketch, "E137.MirrorC", {"center": v(409.3, 30.32) * mm, "radius": 1.13 * mm});
            skCircle(sketch, "E138.MirrorC", {"center": v(524.06, 29.24) * mm, "radius": 1.13 * mm});
            skCircle(sketch, "E139.MirrorC", {"center": v(624.44, 28.3) * mm, "radius": 1.13 * mm});
            skSolve(sketch);
        }
        {
            var Q0;
            Q0=qSketchRegion(id+"F3",true);
            extrude(context, id + "F4", {"entities" : qUnion([Q0]), "operationType" : NewBodyOperationType.REMOVE, "endBound" : BoundingType.THROUGH_ALL, "depth" : 25.4 * mm});
        }
    });
